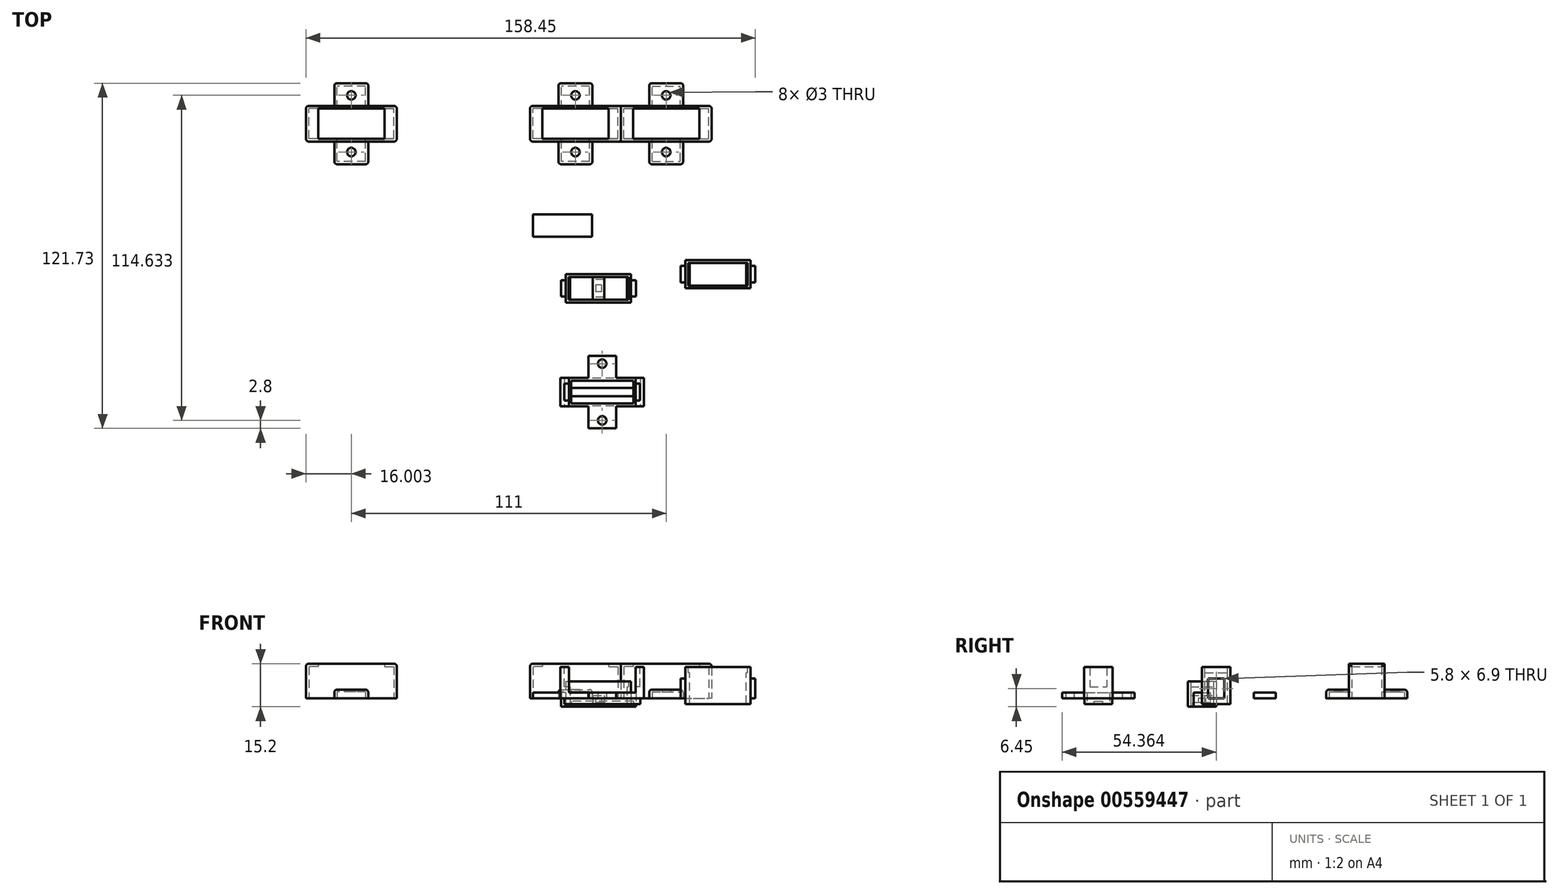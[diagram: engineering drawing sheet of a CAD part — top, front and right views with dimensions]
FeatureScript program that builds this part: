
annotation { "Feature Type Name" : "Feature", "Feature Type Description" : "" }
export const myFeature = defineFeature(function(context is Context, id is Id, definition is map)
    precondition{}
    {
        {
            var Q0;
            Q0=qCreatedBy(makeId("Top.planeOp"),FACE);
            var sketch = newSketch(context, id + "F0", { "sketchPlane" : qUnion([Q0])});
            skLineSegment(sketch, "E0.bottom", {"start": v(-76.87, -5) * mm, "end": v(-104.37, -5) * mm});
            skLineSegment(sketch, "E0.top", {"start": v(-76.87, 5) * mm, "end": v(-104.37, 5) * mm});
            skLineSegment(sketch, "E0.left", {"start": v(-76.87, -5) * mm, "end": v(-76.87, 5) * mm});
            skLineSegment(sketch, "E0.right", {"start": v(-104.37, -5) * mm, "end": v(-104.37, 5) * mm});
            skPoint(sketch, "E0.middle", {"position": v(-90.62, 0) * mm});
            skLineSegment(sketch, "E1.bottom", {"start": v(-87.02, -3.6) * mm, "end": v(-94.22, -3.6) * mm, "construction": true});
            skLineSegment(sketch, "E1.top", {"start": v(-87.02, 3.6) * mm, "end": v(-94.22, 3.6) * mm, "construction": true});
            skLineSegment(sketch, "E1.left", {"start": v(-87.02, -3.6) * mm, "end": v(-87.02, 3.6) * mm, "construction": true});
            skLineSegment(sketch, "E1.right", {"start": v(-94.22, -3.6) * mm, "end": v(-94.22, 3.6) * mm, "construction": true});
            skPoint(sketch, "E2", {"position": v(-90.62, -2.75) * mm});
            skPoint(sketch, "E3", {"position": v(-90.62, 2.75) * mm});
            skLineSegment(sketch, "E4.bottom", {"start": v(-79.62, -4) * mm, "end": v(-101.62, -4) * mm});
            skLineSegment(sketch, "E4.top", {"start": v(-79.62, -1.5) * mm, "end": v(-101.62, -1.5) * mm});
            skLineSegment(sketch, "E4.left", {"start": v(-79.62, -4) * mm, "end": v(-79.62, -1.5) * mm});
            skLineSegment(sketch, "E4.right", {"start": v(-101.62, -4) * mm, "end": v(-101.62, -1.5) * mm});
            skLineSegment(sketch, "E5.bottom", {"start": v(-79.62, 1.5) * mm, "end": v(-101.62, 1.5) * mm});
            skLineSegment(sketch, "E5.top", {"start": v(-79.62, 4) * mm, "end": v(-101.62, 4) * mm});
            skLineSegment(sketch, "E5.left", {"start": v(-79.62, 1.5) * mm, "end": v(-79.62, 4) * mm});
            skLineSegment(sketch, "E5.right", {"start": v(-101.62, 1.5) * mm, "end": v(-101.62, 4) * mm});
            skCircle(sketch, "E6", {"center": v(-90.62, 10) * mm, "radius": 1.5 * mm});
            skCircle(sketch, "E7", {"center": v(-90.62, -10) * mm, "radius": 1.5 * mm});
            skLineSegment(sketch, "E8.bottom", {"start": v(-80.62, -2.5) * mm, "end": v(-85.62, -2.5) * mm, "construction": true});
            skLineSegment(sketch, "E8.top", {"start": v(-80.62, 2.5) * mm, "end": v(-85.62, 2.5) * mm, "construction": true});
            skLineSegment(sketch, "E8.left", {"start": v(-80.62, -2.5) * mm, "end": v(-80.62, 2.5) * mm, "construction": true});
            skLineSegment(sketch, "E8.right", {"start": v(-85.62, -2.5) * mm, "end": v(-85.62, 2.5) * mm, "construction": true});
            skPoint(sketch, "E8.middle", {"position": v(-83.12, 0) * mm});
            skLineSegment(sketch, "E9.bottom", {"start": v(-95.62, -2.5) * mm, "end": v(-100.62, -2.5) * mm, "construction": true});
            skLineSegment(sketch, "E9.top", {"start": v(-95.62, 2.5) * mm, "end": v(-100.62, 2.5) * mm, "construction": true});
            skLineSegment(sketch, "E9.left", {"start": v(-95.62, -2.5) * mm, "end": v(-95.62, 2.5) * mm, "construction": true});
            skLineSegment(sketch, "E9.right", {"start": v(-100.62, -2.5) * mm, "end": v(-100.62, 2.5) * mm, "construction": true});
            skPoint(sketch, "E9.middle", {"position": v(-98.12, 0) * mm});
            skLineSegment(sketch, "E10.bottom", {"start": v(-104.37, 5) * mm, "end": v(-105.37, 5) * mm});
            skLineSegment(sketch, "E10.top", {"start": v(-104.37, -5) * mm, "end": v(-105.37, -5) * mm});
            skLineSegment(sketch, "E10.left", {"start": v(-104.37, 5) * mm, "end": v(-104.37, -5) * mm});
            skLineSegment(sketch, "E10.right", {"start": v(-105.37, 5) * mm, "end": v(-105.37, -5) * mm});
            skLineSegment(sketch, "E11.bottom", {"start": v(-76.87, 5) * mm, "end": v(-75.87, 5) * mm});
            skLineSegment(sketch, "E11.top", {"start": v(-76.87, -5) * mm, "end": v(-75.87, -5) * mm});
            skLineSegment(sketch, "E11.left", {"start": v(-76.87, 5) * mm, "end": v(-76.87, -5) * mm});
            skLineSegment(sketch, "E11.right", {"start": v(-75.87, 5) * mm, "end": v(-75.87, -5) * mm});
            skLineSegment(sketch, "E12.bottom", {"start": v(-95.52, 5) * mm, "end": v(-85.72, 5) * mm});
            skLineSegment(sketch, "E12.top", {"start": v(-95.52, 12.8) * mm, "end": v(-85.72, 12.8) * mm});
            skLineSegment(sketch, "E12.left", {"start": v(-95.52, 5) * mm, "end": v(-95.52, 12.8) * mm});
            skLineSegment(sketch, "E12.right", {"start": v(-85.72, 5) * mm, "end": v(-85.72, 12.8) * mm});
            skLineSegment(sketch, "E13.bottom", {"start": v(-95.52, -5) * mm, "end": v(-85.72, -5) * mm});
            skLineSegment(sketch, "E13.top", {"start": v(-95.52, -12.8) * mm, "end": v(-85.72, -12.8) * mm});
            skLineSegment(sketch, "E13.left", {"start": v(-95.52, -5) * mm, "end": v(-95.52, -12.8) * mm});
            skLineSegment(sketch, "E13.right", {"start": v(-85.72, -5) * mm, "end": v(-85.72, -12.8) * mm});
            skSolve(sketch);
        }
        {
            var Q0;
            Q0=qCreatedBy(makeId("Top.planeOp"),FACE);
            var sketch = newSketch(context, id + "F1", { "sketchPlane" : qUnion([Q0])});
            skLineSegment(sketch, "E14.bottom", {"start": v(-67.93, -50.25) * mm, "end": v(-77.68, -50.25) * mm});
            skLineSegment(sketch, "E14.top", {"start": v(-67.93, -37.75) * mm, "end": v(-77.68, -37.75) * mm});
            skLineSegment(sketch, "E14.left", {"start": v(-67.93, -50.25) * mm, "end": v(-67.93, -37.75) * mm});
            skLineSegment(sketch, "E14.right", {"start": v(-95.43, -50.25) * mm, "end": v(-95.43, -37.75) * mm});
            skPoint(sketch, "E14.middle", {"position": v(-81.68, -44) * mm});
            skCircle(sketch, "E15", {"center": v(-81.68, -34) * mm, "radius": 1.5 * mm});
            skCircle(sketch, "E16", {"center": v(-81.68, -54) * mm, "radius": 1.5 * mm});
            skLineSegment(sketch, "E17.0", {"start": v(-66.93, -51.25) * mm, "end": v(-76.68, -51.25) * mm});
            skLineSegment(sketch, "E17.1", {"start": v(-66.93, -51.25) * mm, "end": v(-66.93, -36.75) * mm});
            skLineSegment(sketch, "E17.2", {"start": v(-66.93, -36.75) * mm, "end": v(-76.68, -36.75) * mm});
            skLineSegment(sketch, "E17.3", {"start": v(-96.43, -51.25) * mm, "end": v(-96.43, -36.75) * mm});
            skLineSegment(sketch, "E18.top", {"start": v(-86.68, -30.75) * mm, "end": v(-76.68, -30.75) * mm});
            skLineSegment(sketch, "E18.left", {"start": v(-86.68, -36.75) * mm, "end": v(-86.68, -30.75) * mm});
            skLineSegment(sketch, "E18.right", {"start": v(-76.68, -36.75) * mm, "end": v(-76.68, -30.75) * mm});
            skLineSegment(sketch, "E19.top", {"start": v(-86.68, -57.25) * mm, "end": v(-76.68, -57.25) * mm});
            skLineSegment(sketch, "E19.left", {"start": v(-86.68, -51.25) * mm, "end": v(-86.68, -57.25) * mm});
            skLineSegment(sketch, "E19.right", {"start": v(-76.68, -51.25) * mm, "end": v(-76.68, -57.25) * mm});
            skPoint(sketch, "E20", {"position": v(-81.68, -30.75) * mm});
            skLineSegment(sketch, "E21.bottom", {"start": v(-86.68, -57.25) * mm, "end": v(-85.68, -57.25) * mm});
            skLineSegment(sketch, "E21.left", {"start": v(-86.68, -57.25) * mm, "end": v(-86.68, -51.25) * mm});
            skLineSegment(sketch, "E21.right", {"start": v(-85.68, -56.25) * mm, "end": v(-85.68, -50.25) * mm});
            skLineSegment(sketch, "E22.bottom", {"start": v(-76.68, -57.25) * mm, "end": v(-77.68, -57.25) * mm});
            skLineSegment(sketch, "E22.left", {"start": v(-76.68, -57.25) * mm, "end": v(-76.68, -51.25) * mm});
            skLineSegment(sketch, "E22.right", {"start": v(-77.68, -56.25) * mm, "end": v(-77.68, -50.25) * mm});
            skLineSegment(sketch, "E23.bottom", {"start": v(-85.68, -57.25) * mm, "end": v(-77.68, -57.25) * mm});
            skLineSegment(sketch, "E23.top", {"start": v(-85.68, -56.25) * mm, "end": v(-77.68, -56.25) * mm});
            skLineSegment(sketch, "E24.trimOffspring", {"start": v(-86.68, -51.25) * mm, "end": v(-96.43, -51.25) * mm});
            skLineSegment(sketch, "E25.trimOffspring", {"start": v(-85.68, -50.25) * mm, "end": v(-95.43, -50.25) * mm});
            skLineSegment(sketch, "E26.left", {"start": v(-86.68, -30.75) * mm, "end": v(-86.68, -36.75) * mm});
            skLineSegment(sketch, "E26.right", {"start": v(-85.68, -31.75) * mm, "end": v(-85.68, -37.75) * mm});
            skLineSegment(sketch, "E27.left", {"start": v(-76.68, -30.75) * mm, "end": v(-76.68, -36.75) * mm});
            skLineSegment(sketch, "E27.right", {"start": v(-77.68, -31.75) * mm, "end": v(-77.68, -37.75) * mm});
            skLineSegment(sketch, "E28.bottom", {"start": v(-85.68, -30.75) * mm, "end": v(-77.68, -30.75) * mm});
            skLineSegment(sketch, "E28.top", {"start": v(-85.68, -31.75) * mm, "end": v(-77.68, -31.75) * mm});
            skLineSegment(sketch, "E29.trimOffspring", {"start": v(-86.68, -36.75) * mm, "end": v(-96.43, -36.75) * mm});
            skLineSegment(sketch, "E30.trimOffspring", {"start": v(-85.68, -37.75) * mm, "end": v(-95.43, -37.75) * mm});
            skLineSegment(sketch, "E31.0", {"start": v(-84.05, 88.33) * mm, "end": v(-84.05, 100.93) * mm});
            skLineSegment(sketch, "E31.1", {"start": v(-106.05, 88.33) * mm, "end": v(-116.05, 88.33) * mm});
            skLineSegment(sketch, "E31.2", {"start": v(-106.05, 80.33) * mm, "end": v(-106.05, 88.33) * mm});
            skLineSegment(sketch, "E31.3", {"start": v(-94.05, 80.33) * mm, "end": v(-106.05, 80.33) * mm});
            skLineSegment(sketch, "E31.4", {"start": v(-94.05, 80.33) * mm, "end": v(-94.05, 88.33) * mm});
            skLineSegment(sketch, "E31.5", {"start": v(-116.05, 88.33) * mm, "end": v(-116.05, 100.93) * mm});
            skLineSegment(sketch, "E31.6", {"start": v(-84.05, 88.33) * mm, "end": v(-94.05, 88.33) * mm});
            skLineSegment(sketch, "E31.7", {"start": v(-106.05, 100.93) * mm, "end": v(-116.05, 100.93) * mm});
            skLineSegment(sketch, "E31.8", {"start": v(-106.05, 100.93) * mm, "end": v(-106.05, 108.93) * mm});
            skLineSegment(sketch, "E31.9", {"start": v(-94.05, 108.93) * mm, "end": v(-106.05, 108.93) * mm});
            skLineSegment(sketch, "E31.10", {"start": v(-94.05, 100.93) * mm, "end": v(-94.05, 108.93) * mm});
            skLineSegment(sketch, "E31.11", {"start": v(-84.05, 100.93) * mm, "end": v(-94.05, 100.93) * mm});
            skPoint(sketch, "E32", {"position": v(-100.05, 94.63) * mm});
            skPoint(sketch, "E32.positionSnap0", {"position": v(-100.05, 108.93) * mm});
            skPoint(sketch, "E32.positionSnap1", {"position": v(-116.05, 94.63) * mm});
            skSolve(sketch);
        }
        {
            var Q0;
            Q0=makeQuery(id+"F0.imprint","IMPRINT",FACE,{"disambiguationData":[TD([[makeQuery(id+"F0.imprint","IMPRINT",EDGE,{"derivedFrom":sQuery(id+"F0.wireOp",EDGE,"E0.bottom")}),-1.0]])]});
            var Q1;
            {var subQ1=sQuery(id+"F0.wireOp",EDGE,"E10.bottom");Q1=makeQuery(id+"F0.imprint","IMPRINT",FACE,{"disambiguationData":[TD([[makeQuery(id+"F0.imprint","IMPRINT",EDGE,{"derivedFrom":subQ1}),1.0]])]});}
            var Q2;
            {var subQ1=sQuery(id+"F0.wireOp",EDGE,"E11.bottom");Q2=makeQuery(id+"F0.imprint","IMPRINT",FACE,{"disambiguationData":[TD([[makeQuery(id+"F0.imprint","IMPRINT",EDGE,{"derivedFrom":subQ1}),-1.0]])]});}
            var Q3;
            Q3=makeQuery(id+"F0.imprint","IMPRINT",FACE,{"disambiguationData":[TD([[makeQuery(id+"F0.imprint","IMPRINT",EDGE,{"derivedFrom":sQuery(id+"F0.wireOp",EDGE,"E6")}),-1.0]])]});
            var Q4;
            Q4=makeQuery(id+"F0.imprint","IMPRINT",FACE,{"disambiguationData":[TD([[makeQuery(id+"F0.imprint","IMPRINT",EDGE,{"derivedFrom":sQuery(id+"F0.wireOp",EDGE,"E7")}),-1.0]])]});
            extrude(context, id + "F2", {"entities" : qUnion([Q0, Q1, Q2, Q3, Q4]), "depth" : 1 * mm});
        }
        {
            var Q0;
            Q0=makeQuery(id+"F2.opExtrude","CAP_FACE",FACE,{"disambiguationData":[OSD([sQuery(id+"F0.wireOp",EDGE,"E0.bottom"),sQuery(id+"F0.wireOp",EDGE,"E0.top"),sQuery(id+"F0.wireOp",EDGE,"E0.left"),sQuery(id+"F0.wireOp",EDGE,"E0.right"),sQuery(id+"F0.wireOp",EDGE,"E4.bottom"),sQuery(id+"F0.wireOp",EDGE,"E4.top"),sQuery(id+"F0.wireOp",EDGE,"E4.left"),sQuery(id+"F0.wireOp",EDGE,"E4.right"),sQuery(id+"F0.wireOp",EDGE,"E5.bottom"),sQuery(id+"F0.wireOp",EDGE,"E5.top"),sQuery(id+"F0.wireOp",EDGE,"E5.left"),sQuery(id+"F0.wireOp",EDGE,"E5.right"),sQuery(id+"F0.wireOp",EDGE,"E6"),sQuery(id+"F0.wireOp",EDGE,"E7")])],"isStart":false});
            var sketch = newSketch(context, id + "F3", { "sketchPlane" : qUnion([Q0])});
            skLineSegment(sketch, "E33.bottom", {"start": v(-105.37, -5) * mm, "end": v(-102.37, -5) * mm});
            skLineSegment(sketch, "E33.top", {"start": v(-105.37, 5) * mm, "end": v(-102.37, 5) * mm});
            skLineSegment(sketch, "E33.left", {"start": v(-105.37, -5) * mm, "end": v(-105.37, 5) * mm});
            skLineSegment(sketch, "E33.right", {"start": v(-102.37, -5) * mm, "end": v(-102.37, 5) * mm});
            skLineSegment(sketch, "E34.bottom", {"start": v(-75.87, 5) * mm, "end": v(-78.87, 5) * mm});
            skLineSegment(sketch, "E34.top", {"start": v(-75.87, -5) * mm, "end": v(-78.87, -5) * mm});
            skLineSegment(sketch, "E34.left", {"start": v(-75.87, 5) * mm, "end": v(-75.87, -5) * mm});
            skLineSegment(sketch, "E34.right", {"start": v(-78.87, 5) * mm, "end": v(-78.87, -5) * mm});
            skSolve(sketch);
        }
        {
            var Q0;
            Q0=makeQuery(id+"F1.imprint","IMPRINT",FACE,{"disambiguationData":[TD([[makeQuery(id+"F1.imprint","IMPRINT",EDGE,{"derivedFrom":sQuery(id+"F1.wireOp",EDGE,"E31.0")}),1.0]])]});
            extrude(context, id + "F4", {"entities" : qUnion([Q0]), "depth" : 12.2 * mm});
        }
        {
            var Q0;
            Q0=makeQuery(id+"F4.opExtrude","CAP_FACE",FACE,{"disambiguationData":[OSD([sQuery(id+"F1.wireOp",EDGE,"E31.0"),sQuery(id+"F1.wireOp",EDGE,"E31.1"),sQuery(id+"F1.wireOp",EDGE,"E31.2"),sQuery(id+"F1.wireOp",EDGE,"E31.3"),sQuery(id+"F1.wireOp",EDGE,"E31.4"),sQuery(id+"F1.wireOp",EDGE,"E31.5"),sQuery(id+"F1.wireOp",EDGE,"E31.6"),sQuery(id+"F1.wireOp",EDGE,"E31.7"),sQuery(id+"F1.wireOp",EDGE,"E31.8"),sQuery(id+"F1.wireOp",EDGE,"E31.9"),sQuery(id+"F1.wireOp",EDGE,"E31.10"),sQuery(id+"F1.wireOp",EDGE,"E31.11")])],"isStart":true});
            shell(context, id + "F5", {"entities" : qUnion([Q0]), "thickness" : 1 * mm});
        }
        {
            var Q0;
            Q0=makeQuery(id+"F4.opExtrude","CAP_FACE",FACE,{"disambiguationData":[OSD([sQuery(id+"F1.wireOp",EDGE,"E31.0"),sQuery(id+"F1.wireOp",EDGE,"E31.1"),sQuery(id+"F1.wireOp",EDGE,"E31.2"),sQuery(id+"F1.wireOp",EDGE,"E31.3"),sQuery(id+"F1.wireOp",EDGE,"E31.4"),sQuery(id+"F1.wireOp",EDGE,"E31.5"),sQuery(id+"F1.wireOp",EDGE,"E31.6"),sQuery(id+"F1.wireOp",EDGE,"E31.7"),sQuery(id+"F1.wireOp",EDGE,"E31.8"),sQuery(id+"F1.wireOp",EDGE,"E31.9"),sQuery(id+"F1.wireOp",EDGE,"E31.10"),sQuery(id+"F1.wireOp",EDGE,"E31.11")])],"isStart":false});
            var sketch = newSketch(context, id + "F6", { "sketchPlane" : qUnion([Q0])});
            skLineSegment(sketch, "E35.bottom", {"start": v(-110.05, 109.64) * mm, "end": v(-85.3, 109.64) * mm});
            skLineSegment(sketch, "E35.top", {"start": v(-110.05, 100.93) * mm, "end": v(-85.3, 100.93) * mm});
            skLineSegment(sketch, "E35.left", {"start": v(-110.05, 109.64) * mm, "end": v(-110.05, 100.93) * mm});
            skLineSegment(sketch, "E35.right", {"start": v(-85.3, 109.64) * mm, "end": v(-85.3, 100.93) * mm});
            skLineSegment(sketch, "E36.bottom", {"start": v(-110.05, 88.33) * mm, "end": v(-90.05, 88.33) * mm});
            skLineSegment(sketch, "E36.top", {"start": v(-110.05, 79.54) * mm, "end": v(-90.05, 79.54) * mm});
            skLineSegment(sketch, "E36.left", {"start": v(-110.05, 88.33) * mm, "end": v(-110.05, 79.54) * mm});
            skLineSegment(sketch, "E36.right", {"start": v(-90.05, 88.33) * mm, "end": v(-90.05, 79.54) * mm});
            skSolve(sketch);
        }
        {
            var Q0;
            Q0=makeQuery(id+"F6.imprint","IMPRINT",FACE,{"disambiguationData":[TD([[makeQuery(id+"F6.imprint","IMPRINT",EDGE,{"derivedFrom":sQuery(id+"F6.wireOp",EDGE,"E36.top")}),1.0]])]});
            var Q1;
            Q1=makeQuery(id+"F6.imprint","IMPRINT",FACE,{"disambiguationData":[TD([[makeQuery(id+"F6.imprint","IMPRINT",EDGE,{"derivedFrom":sQuery(id+"F6.wireOp",EDGE,"E35.bottom")}),-1.0]])]});
            var Q2;
            {var subQ1=makeQuery(id+"F4.opExtrude","CAP_EDGE",EDGE,{"disambiguationData":[OSD([sQuery(id+"F1.wireOp",EDGE,"E31.8")])],"isStart":false});Q2=makeQuery(id+"F6.imprint","IMPRINT",FACE,{"disambiguationData":[TD([[makeQuery(id+"F6.imprint","IMPRINT",EDGE,{"derivedFrom":subQ1}),-1.0]])]});}
            var Q3;
            {var subQ1=makeQuery(id+"F4.opExtrude","CAP_EDGE",EDGE,{"disambiguationData":[OSD([sQuery(id+"F1.wireOp",EDGE,"E31.2")])],"isStart":false});Q3=makeQuery(id+"F6.imprint","IMPRINT",FACE,{"disambiguationData":[TD([[makeQuery(id+"F6.imprint","IMPRINT",EDGE,{"derivedFrom":subQ1}),-1.0]])]});}
            extrude(context, id + "F7", {"entities" : qUnion([Q0, Q1, Q2, Q3]), "operationType" : NewBodyOperationType.REMOVE, "oppositeDirection" : true, "depth" : 11.2 * mm});
        }
        {
            var Q0;
            Q0=makeQuery(id+"F5.opShell","OFFSET_FACE",FACE,{"disambiguationData":[OSD([sQuery(id+"F1.wireOp",EDGE,"E31.4")])]});
            var sketch = newSketch(context, id + "F8", { "sketchPlane" : qUnion([Q0])});
            skLineSegment(sketch, "E37.bottom", {"start": v(-88.33, 11.2) * mm, "end": v(-89.33, 11.2) * mm});
            skLineSegment(sketch, "E37.top", {"start": v(-88.33, 0) * mm, "end": v(-89.33, 0) * mm});
            skLineSegment(sketch, "E37.left", {"start": v(-88.33, 11.2) * mm, "end": v(-88.33, 0) * mm});
            skLineSegment(sketch, "E37.right", {"start": v(-89.33, 11.2) * mm, "end": v(-89.33, 0) * mm});
            skSolve(sketch);
        }
        {
            var Q0;
            Q0=makeQuery(id+"F5.opShell","OFFSET_FACE",FACE,{"disambiguationData":[OSD([sQuery(id+"F1.wireOp",EDGE,"E31.10")])]});
            var sketch = newSketch(context, id + "F9", { "sketchPlane" : qUnion([Q0])});
            skLineSegment(sketch, "E38.bottom", {"start": v(-99.93, 11.2) * mm, "end": v(-100.93, 11.2) * mm});
            skLineSegment(sketch, "E38.top", {"start": v(-99.93, 0) * mm, "end": v(-100.93, 0) * mm});
            skLineSegment(sketch, "E38.left", {"start": v(-99.93, 11.2) * mm, "end": v(-99.93, 0) * mm});
            skLineSegment(sketch, "E38.right", {"start": v(-100.93, 11.2) * mm, "end": v(-100.93, 0) * mm});
            skSolve(sketch);
        }
        {
            var Q0;
            Q0=qSketchRegion(id+"F9",true);
            var Q1;
            {var subQ1=sQuery(id+"F8.wireOp",EDGE,"E37.bottom");Q1=makeQuery(id+"F8.imprint","IMPRINT",FACE,{"disambiguationData":[TD([[makeQuery(id+"F8.imprint","IMPRINT",EDGE,{"derivedFrom":subQ1}),1.0]])]});}
            extrude(context, id + "F10", {"entities" : qUnion([Q0, Q1]), "operationType" : NewBodyOperationType.ADD, "depth" : 16 * mm});
        }
        {
            var Q0;
            Q0=makeQuery(id+"F4.opExtrude","CAP_FACE",FACE,{"disambiguationData":[OSD([sQuery(id+"F1.wireOp",EDGE,"E31.0"),sQuery(id+"F1.wireOp",EDGE,"E31.1"),sQuery(id+"F1.wireOp",EDGE,"E31.2"),sQuery(id+"F1.wireOp",EDGE,"E31.3"),sQuery(id+"F1.wireOp",EDGE,"E31.4"),sQuery(id+"F1.wireOp",EDGE,"E31.5"),sQuery(id+"F1.wireOp",EDGE,"E31.6"),sQuery(id+"F1.wireOp",EDGE,"E31.7"),sQuery(id+"F1.wireOp",EDGE,"E31.8"),sQuery(id+"F1.wireOp",EDGE,"E31.9"),sQuery(id+"F1.wireOp",EDGE,"E31.10"),sQuery(id+"F1.wireOp",EDGE,"E31.11")])],"isStart":false});
            var sketch = newSketch(context, id + "F11", { "sketchPlane" : qUnion([Q0])});
            skLineSegment(sketch, "E39.bottom", {"start": v(-85.05, 89.33) * mm, "end": v(-115.05, 89.33) * mm});
            skLineSegment(sketch, "E39.top", {"start": v(-85.05, 99.93) * mm, "end": v(-115.05, 99.93) * mm});
            skLineSegment(sketch, "E39.left", {"start": v(-85.05, 89.33) * mm, "end": v(-85.05, 99.93) * mm});
            skLineSegment(sketch, "E39.right", {"start": v(-115.05, 89.33) * mm, "end": v(-115.05, 99.93) * mm});
            skPoint(sketch, "E39.middle", {"position": v(-100.05, 94.63) * mm});
            skPoint(sketch, "E40.positionSnap0", {"position": v(-100.05, 101.88) * mm});
            skPoint(sketch, "E40.positionSnap1", {"position": v(-116.05, 94.63) * mm});
            skSolve(sketch);
        }
        {
            var Q0;
            Q0=makeQuery(id+"F11.imprint","IMPRINT",FACE,{"disambiguationData":[TD([[makeQuery(id+"F11.imprint","IMPRINT",EDGE,{"derivedFrom":sQuery(id+"F11.wireOp",EDGE,"E39.bottom")}),-1.0]])]});
            extrude(context, id + "F12", {"entities" : qUnion([Q0]), "operationType" : NewBodyOperationType.REMOVE, "oppositeDirection" : true, "depth" : 25 * mm});
        }
        {
            var Q0;
            Q0=makeQuery(id+"F7.boolean.opBoolean","COPY",FACE,{"derivedFrom":makeQuery(id+"F7.opExtrude","CAP_FACE",FACE,{"disambiguationData":[OSD([sQuery(id+"F6.wireOp",EDGE,"E35.bottom"),sQuery(id+"F6.wireOp",EDGE,"E35.top"),sQuery(id+"F6.wireOp",EDGE,"E35.left"),sQuery(id+"F6.wireOp",EDGE,"E35.right")])],"isStart":false})});
            var sketch = newSketch(context, id + "F13", { "sketchPlane" : qUnion([Q0])});
            skLineSegment(sketch, "E41.bottom", {"start": v(-106.05, 108.93) * mm, "end": v(-94.05, 108.93) * mm});
            skLineSegment(sketch, "E41.top", {"start": v(-106.05, 100.93) * mm, "end": v(-94.05, 100.93) * mm});
            skLineSegment(sketch, "E41.left", {"start": v(-106.05, 108.93) * mm, "end": v(-106.05, 100.93) * mm});
            skLineSegment(sketch, "E41.right", {"start": v(-94.05, 108.93) * mm, "end": v(-94.05, 100.93) * mm});
            skLineSegment(sketch, "E42.bottom", {"start": v(-106.05, 80.33) * mm, "end": v(-94.05, 80.33) * mm});
            skLineSegment(sketch, "E42.top", {"start": v(-106.05, 88.33) * mm, "end": v(-94.05, 88.33) * mm});
            skLineSegment(sketch, "E42.left", {"start": v(-106.05, 80.33) * mm, "end": v(-106.05, 88.33) * mm});
            skLineSegment(sketch, "E42.right", {"start": v(-94.05, 80.33) * mm, "end": v(-94.05, 88.33) * mm});
            skCircle(sketch, "E43", {"center": v(-100.05, 104.63) * mm, "radius": 1.5 * mm});
            skPoint(sketch, "E43.centerSnap0", {"position": v(-100.05, 108.93) * mm});
            skCircle(sketch, "E44", {"center": v(-100.05, 84.63) * mm, "radius": 1.5 * mm});
            skCircle(sketch, "E45", {"center": v(-100.05, 84.63) * mm, "radius": 2.75 * mm, "construction": true});
            skCircle(sketch, "E46", {"center": v(-100.05, 104.63) * mm, "radius": 2.75 * mm, "construction": true});
            skSolve(sketch);
        }
        {
            var Q0;
            Q0=makeQuery(id+"F13.imprint","IMPRINT",FACE,{"disambiguationData":[TD([[makeQuery(id+"F13.imprint","IMPRINT",EDGE,{"derivedFrom":sQuery(id+"F13.wireOp",EDGE,"E43")}),-1.0]])]});
            var Q1;
            Q1=makeQuery(id+"F13.imprint","IMPRINT",FACE,{"disambiguationData":[TD([[makeQuery(id+"F13.imprint","IMPRINT",EDGE,{"derivedFrom":sQuery(id+"F13.wireOp",EDGE,"E41.bottom")}),1.0]])]});
            var Q2;
            Q2=makeQuery(id+"F13.imprint","IMPRINT",FACE,{"disambiguationData":[TD([[makeQuery(id+"F13.imprint","IMPRINT",EDGE,{"derivedFrom":sQuery(id+"F13.wireOp",EDGE,"E42.bottom")}),1.0]])]});
            extrude(context, id + "F14", {"entities" : qUnion([Q0, Q1, Q2]), "operationType" : NewBodyOperationType.ADD, "depth" : 2 * mm});
        }
        {
            var Q0;
            Q0=makeQuery(id+"F1.imprint","IMPRINT",FACE,{"disambiguationData":[TD([[makeQuery(id+"F1.imprint","IMPRINT",EDGE,{"derivedFrom":sQuery(id+"F1.wireOp",EDGE,"E31.0")}),1.0]])]});
            var sketch = newSketch(context, id + "F15", { "sketchPlane" : qUnion([Q0])});
            skLineSegment(sketch, "E47.bottom", {"start": v(-105.05, 81.33) * mm, "end": v(-95.05, 81.33) * mm});
            skLineSegment(sketch, "E47.top", {"start": v(-105.05, 107.93) * mm, "end": v(-95.05, 107.93) * mm});
            skLineSegment(sketch, "E47.left", {"start": v(-105.05, 81.33) * mm, "end": v(-105.05, 107.93) * mm});
            skLineSegment(sketch, "E47.right", {"start": v(-95.05, 81.33) * mm, "end": v(-95.05, 107.93) * mm});
            skPoint(sketch, "E48.0", {"position": v(-105.05, 107.93) * mm});
            skSolve(sketch);
        }
        {
            var Q0;
            Q0=makeQuery(id+"F15.imprint","IMPRINT",FACE,{"disambiguationData":[TD([[makeQuery(id+"F15.imprint","IMPRINT",EDGE,{"derivedFrom":sQuery(id+"F15.wireOp",EDGE,"E47.bottom")}),1.0]])]});
            extrude(context, id + "F16", {"entities" : qUnion([Q0]), "operationType" : NewBodyOperationType.REMOVE, "depth" : 2.2 * mm});
        }
        {
            var Q0;
            Q0=makeQuery(id+"F12.boolean.opBoolean","MERGE",FACE,{"derivedFrom":[makeQuery(id+"F5.opShell","OFFSET_FACE",FACE,{"disambiguationData":[OSD([sQuery(id+"F1.wireOp",EDGE,"E31.5")])]}),makeQuery(id+"F12.opExtrude","SWEPT_FACE",FACE,{"disambiguationData":[OSD([sQuery(id+"F11.wireOp",EDGE,"E39.right")])]})]});
            var sketch = newSketch(context, id + "F17", { "sketchPlane" : qUnion([Q0])});
            skLineSegment(sketch, "E49.bottom", {"start": v(89.33, 11.2) * mm, "end": v(99.93, 11.2) * mm});
            skLineSegment(sketch, "E49.top", {"start": v(89.33, 12.2) * mm, "end": v(99.93, 12.2) * mm});
            skLineSegment(sketch, "E49.left", {"start": v(89.33, 11.2) * mm, "end": v(89.33, 12.2) * mm});
            skLineSegment(sketch, "E49.right", {"start": v(99.93, 11.2) * mm, "end": v(99.93, 12.2) * mm});
            skSolve(sketch);
        }
        {
            var Q0;
            Q0=makeQuery(id+"F12.boolean.opBoolean","MERGE",FACE,{"derivedFrom":[makeQuery(id+"F5.opShell","OFFSET_FACE",FACE,{"disambiguationData":[OSD([sQuery(id+"F1.wireOp",EDGE,"E31.0")])]}),makeQuery(id+"F12.opExtrude","SWEPT_FACE",FACE,{"disambiguationData":[OSD([sQuery(id+"F11.wireOp",EDGE,"E39.left")])]})]});
            var sketch = newSketch(context, id + "F18", { "sketchPlane" : qUnion([Q0])});
            skLineSegment(sketch, "E50.bottom", {"start": v(-99.93, 11.2) * mm, "end": v(-89.33, 11.2) * mm});
            skLineSegment(sketch, "E50.top", {"start": v(-99.93, 12.2) * mm, "end": v(-89.33, 12.2) * mm});
            skLineSegment(sketch, "E50.left", {"start": v(-99.93, 11.2) * mm, "end": v(-99.93, 12.2) * mm});
            skLineSegment(sketch, "E50.right", {"start": v(-89.33, 11.2) * mm, "end": v(-89.33, 12.2) * mm});
            skSolve(sketch);
        }
        {
            var Q0;
            Q0=makeQuery(id+"F17.imprint","IMPRINT",FACE,{"disambiguationData":[TD([[makeQuery(id+"F17.imprint","IMPRINT",EDGE,{"derivedFrom":sQuery(id+"F17.wireOp",EDGE,"E49.bottom")}),1.0]])]});
            extrude(context, id + "F19", {"entities" : qUnion([Q0]), "operationType" : NewBodyOperationType.ADD, "depth" : 3.3 * mm});
        }
        {
            var Q0;
            Q0=makeQuery(id+"F18.imprint","IMPRINT",FACE,{"disambiguationData":[TD([[makeQuery(id+"F18.imprint","IMPRINT",EDGE,{"derivedFrom":sQuery(id+"F18.wireOp",EDGE,"E50.bottom")}),1.0]])]});
            extrude(context, id + "F20", {"entities" : qUnion([Q0]), "operationType" : NewBodyOperationType.ADD, "depth" : 3.3 * mm});
        }
        {
            var Q0;
            Q0=makeQuery(id+"F0.imprint","IMPRINT",FACE,{"disambiguationData":[TD([[makeQuery(id+"F0.imprint","IMPRINT",EDGE,{"derivedFrom":sQuery(id+"F0.wireOp",EDGE,"E4.bottom")}),1.0]])]});
            var sketch = newSketch(context, id + "F21", { "sketchPlane" : qUnion([Q0])});
            skPoint(sketch, "E51.0", {"position": v(-90.62, 0) * mm});
            skLineSegment(sketch, "E52.bottom", {"start": v(-77.22, 4.9) * mm, "end": v(-104.02, 4.9) * mm});
            skLineSegment(sketch, "E52.top", {"start": v(-77.22, -4.9) * mm, "end": v(-104.02, -4.9) * mm});
            skLineSegment(sketch, "E52.left", {"start": v(-77.22, 4.9) * mm, "end": v(-77.22, -4.9) * mm});
            skLineSegment(sketch, "E52.right", {"start": v(-104.02, 4.9) * mm, "end": v(-104.02, -4.9) * mm});
            skPoint(sketch, "E53.0", {"position": v(-101.62, -4) * mm});
            skPoint(sketch, "E53.1", {"position": v(-79.62, -1.5) * mm});
            skPoint(sketch, "E53.2", {"position": v(-101.62, 1.5) * mm});
            skPoint(sketch, "E53.3", {"position": v(-79.62, 4) * mm});
            skLineSegment(sketch, "E54.bottom", {"start": v(-101.62, -4) * mm, "end": v(-79.62, -4) * mm});
            skLineSegment(sketch, "E54.top", {"start": v(-101.62, -1.5) * mm, "end": v(-79.62, -1.5) * mm});
            skLineSegment(sketch, "E54.left", {"start": v(-101.62, -4) * mm, "end": v(-101.62, -1.5) * mm});
            skLineSegment(sketch, "E54.right", {"start": v(-79.62, -4) * mm, "end": v(-79.62, -1.5) * mm});
            skLineSegment(sketch, "E55.bottom", {"start": v(-101.62, 1.5) * mm, "end": v(-79.62, 1.5) * mm});
            skLineSegment(sketch, "E55.top", {"start": v(-101.62, 4) * mm, "end": v(-79.62, 4) * mm});
            skLineSegment(sketch, "E55.left", {"start": v(-101.62, 1.5) * mm, "end": v(-101.62, 4) * mm});
            skLineSegment(sketch, "E55.right", {"start": v(-79.62, 1.5) * mm, "end": v(-79.62, 4) * mm});
            skSolve(sketch);
        }
        {
            var Q0;
            Q0=qSketchRegion(id+"F21",true);
            extrude(context, id + "F22", {"entities" : qUnion([Q0]), "operationType" : NewBodyOperationType.ADD, "oppositeDirection" : true, "depth" : 2 * mm});
        }
        {
            var Q0;
            Q0=makeQuery(id+"F2.opExtrude","CAP_FACE",FACE,{"disambiguationData":[OSD([sQuery(id+"F0.wireOp",EDGE,"E0.bottom"),sQuery(id+"F0.wireOp",EDGE,"E0.top"),sQuery(id+"F0.wireOp",EDGE,"E4.bottom"),sQuery(id+"F0.wireOp",EDGE,"E4.top"),sQuery(id+"F0.wireOp",EDGE,"E4.left"),sQuery(id+"F0.wireOp",EDGE,"E4.right"),sQuery(id+"F0.wireOp",EDGE,"E5.bottom"),sQuery(id+"F0.wireOp",EDGE,"E5.top"),sQuery(id+"F0.wireOp",EDGE,"E5.left"),sQuery(id+"F0.wireOp",EDGE,"E5.right"),sQuery(id+"F0.wireOp",EDGE,"E6"),sQuery(id+"F0.wireOp",EDGE,"E7"),sQuery(id+"F0.wireOp",EDGE,"E10.bottom"),sQuery(id+"F0.wireOp",EDGE,"E10.top"),sQuery(id+"F0.wireOp",EDGE,"E10.right"),sQuery(id+"F0.wireOp",EDGE,"E11.bottom"),sQuery(id+"F0.wireOp",EDGE,"E11.top"),sQuery(id+"F0.wireOp",EDGE,"E11.right"),sQuery(id+"F0.wireOp",EDGE,"E12.top"),sQuery(id+"F0.wireOp",EDGE,"E12.left"),sQuery(id+"F0.wireOp",EDGE,"E12.right"),sQuery(id+"F0.wireOp",EDGE,"E13.top"),sQuery(id+"F0.wireOp",EDGE,"E13.left"),sQuery(id+"F0.wireOp",EDGE,"E13.right")])],"isStart":false});
            var sketch = newSketch(context, id + "F23", { "sketchPlane" : qUnion([Q0])});
            skLineSegment(sketch, "E56.bottom", {"start": v(-101.62, 4) * mm, "end": v(-79.62, 4) * mm});
            skLineSegment(sketch, "E56.top", {"start": v(-101.62, -4) * mm, "end": v(-79.62, -4) * mm});
            skLineSegment(sketch, "E56.left", {"start": v(-101.62, 4) * mm, "end": v(-101.62, -4) * mm});
            skLineSegment(sketch, "E56.right", {"start": v(-79.62, 4) * mm, "end": v(-79.62, -4) * mm});
            skSolve(sketch);
        }
        {
            var Q0;
            Q0=qSketchRegion(id+"F23",true);
            extrude(context, id + "F24", {"entities" : qUnion([Q0]), "operationType" : NewBodyOperationType.REMOVE, "oppositeDirection" : true, "depth" : 2 * mm});
        }
        {
            var Q0;
            Q0=makeQuery(id+"F3.imprint","IMPRINT",FACE,{"disambiguationData":[TD([[makeQuery(id+"F3.imprint","IMPRINT",EDGE,{"derivedFrom":sQuery(id+"F3.wireOp",EDGE,"E33.bottom")}),-1.0]])]});
            var Q1;
            Q1=makeQuery(id+"F3.imprint","IMPRINT",FACE,{"disambiguationData":[TD([[makeQuery(id+"F3.imprint","IMPRINT",EDGE,{"derivedFrom":sQuery(id+"F3.wireOp",EDGE,"E34.bottom")}),1.0]])]});
            extrude(context, id + "F25", {"entities" : qUnion([Q0, Q1]), "operationType" : NewBodyOperationType.ADD, "depth" : 10 * mm});
        }
        {
            var Q0;
            Q0=makeQuery(id+"F25.opExtrude","CAP_FACE",FACE,{"disambiguationData":[OSD([sQuery(id+"F3.wireOp",EDGE,"E33.bottom"),sQuery(id+"F3.wireOp",EDGE,"E33.top"),sQuery(id+"F3.wireOp",EDGE,"E33.left"),sQuery(id+"F3.wireOp",EDGE,"E33.right")])],"isStart":false});
            var sketch = newSketch(context, id + "F26", { "sketchPlane" : qUnion([Q0])});
            skPoint(sketch, "E57.0", {"position": v(-90.62, 0) * mm});
            skLineSegment(sketch, "E58.bottom", {"start": v(-77.27, -3) * mm, "end": v(-103.97, -3) * mm});
            skLineSegment(sketch, "E58.top", {"start": v(-77.27, 3) * mm, "end": v(-103.97, 3) * mm});
            skLineSegment(sketch, "E58.left", {"start": v(-77.27, -3) * mm, "end": v(-77.27, 3) * mm});
            skLineSegment(sketch, "E58.right", {"start": v(-103.97, -3) * mm, "end": v(-103.97, 3) * mm});
            skSolve(sketch);
        }
        {
            var Q0;
            {var subQ0=sQuery(id+"F26.wireOp",EDGE,"E58.left");Q0=makeQuery(id+"F26.imprint","IMPRINT",FACE,{"disambiguationData":[TD([[makeQuery(id+"F26.imprint","IMPRINT",EDGE,{"derivedFrom":subQ0}),1.0]])]});}
            var Q1;
            {var subQ0=sQuery(id+"F26.wireOp",EDGE,"E58.right");Q1=makeQuery(id+"F26.imprint","IMPRINT",FACE,{"disambiguationData":[TD([[makeQuery(id+"F26.imprint","IMPRINT",EDGE,{"derivedFrom":subQ0}),-1.0]])]});}
            extrude(context, id + "F27", {"entities" : qUnion([Q0, Q1]), "operationType" : NewBodyOperationType.REMOVE, "oppositeDirection" : true, "depth" : 7 * mm});
        }
        {
            var Q0;
            Q0=qCreatedBy(makeId("Top.planeOp"),FACE);
            var sketch = newSketch(context, id + "F28", { "sketchPlane" : qUnion([Q0])});
            skLineSegment(sketch, "E59.bottom", {"start": v(-80.42, 30.57) * mm, "end": v(-103.42, 30.57) * mm});
            skLineSegment(sketch, "E59.top", {"start": v(-80.42, 42.57) * mm, "end": v(-103.42, 42.57) * mm});
            skLineSegment(sketch, "E59.left", {"start": v(-80.42, 30.57) * mm, "end": v(-80.42, 42.57) * mm});
            skLineSegment(sketch, "E59.right", {"start": v(-103.42, 30.57) * mm, "end": v(-103.42, 42.57) * mm});
            skPoint(sketch, "E59.middle", {"position": v(-91.92, 36.57) * mm});
            skLineSegment(sketch, "E60.bottom", {"start": v(-103.42, 33.67) * mm, "end": v(-105.12, 33.67) * mm});
            skLineSegment(sketch, "E60.top", {"start": v(-103.42, 39.47) * mm, "end": v(-105.12, 39.47) * mm});
            skLineSegment(sketch, "E60.left", {"start": v(-103.42, 33.67) * mm, "end": v(-103.42, 39.47) * mm});
            skLineSegment(sketch, "E60.right", {"start": v(-105.12, 33.67) * mm, "end": v(-105.12, 39.47) * mm});
            skPoint(sketch, "E60.middle", {"position": v(-104.27, 36.57) * mm});
            skLineSegment(sketch, "E61.bottom", {"start": v(-78.72, 33.67) * mm, "end": v(-80.42, 33.67) * mm});
            skLineSegment(sketch, "E61.top", {"start": v(-78.72, 39.47) * mm, "end": v(-80.42, 39.47) * mm});
            skLineSegment(sketch, "E61.left", {"start": v(-78.72, 33.67) * mm, "end": v(-78.72, 39.47) * mm});
            skLineSegment(sketch, "E61.right", {"start": v(-80.42, 33.67) * mm, "end": v(-80.42, 39.47) * mm});
            skPoint(sketch, "E61.middle", {"position": v(-79.57, 36.57) * mm});
            skLineSegment(sketch, "E62.bottom", {"start": v(-93.92, 32.57) * mm, "end": v(-101.92, 32.57) * mm});
            skLineSegment(sketch, "E62.top", {"start": v(-93.92, 40.57) * mm, "end": v(-101.92, 40.57) * mm});
            skLineSegment(sketch, "E62.left", {"start": v(-93.92, 32.57) * mm, "end": v(-93.92, 40.57) * mm});
            skLineSegment(sketch, "E62.right", {"start": v(-101.92, 32.57) * mm, "end": v(-101.92, 40.57) * mm});
            skLineSegment(sketch, "E63.bottom", {"start": v(-81.92, 32.57) * mm, "end": v(-89.92, 32.57) * mm});
            skLineSegment(sketch, "E63.top", {"start": v(-81.92, 40.57) * mm, "end": v(-89.92, 40.57) * mm});
            skLineSegment(sketch, "E63.left", {"start": v(-81.92, 32.57) * mm, "end": v(-81.92, 40.57) * mm});
            skLineSegment(sketch, "E63.right", {"start": v(-89.92, 32.57) * mm, "end": v(-89.92, 40.57) * mm});
            skSolve(sketch);
        }
        {
            var Q0;
            {var subQ3=sQuery(id+"F28.wireOp",EDGE,"E59.bottom");Q0=makeQuery(id+"F28.imprint","IMPRINT",FACE,{"disambiguationData":[TD([[makeQuery(id+"F28.imprint","IMPRINT",EDGE,{"derivedFrom":subQ3}),-1.0]])]});}
            var Q1;
            Q1=makeQuery(id+"F28.imprint","IMPRINT",FACE,{"disambiguationData":[TD([[makeQuery(id+"F28.imprint","IMPRINT",EDGE,{"derivedFrom":sQuery(id+"F28.wireOp",EDGE,"E60.bottom")}),-1.0]])]});
            var Q2;
            Q2=makeQuery(id+"F28.imprint","IMPRINT",FACE,{"disambiguationData":[TD([[makeQuery(id+"F28.imprint","IMPRINT",EDGE,{"derivedFrom":sQuery(id+"F28.wireOp",EDGE,"E61.bottom")}),-1.0]])]});
            extrude(context, id + "F29", {"entities" : qUnion([Q0, Q1, Q2]), "depth" : 1 * mm});
        }
        {
            var Q0;
            Q0=makeQuery(id+"F29.opExtrude","CAP_FACE",FACE,{"disambiguationData":[OSD([sQuery(id+"F28.wireOp",EDGE,"E59.bottom"),sQuery(id+"F28.wireOp",EDGE,"E59.top"),sQuery(id+"F28.wireOp",EDGE,"E59.left"),sQuery(id+"F28.wireOp",EDGE,"E59.right"),sQuery(id+"F28.wireOp",EDGE,"E60.bottom"),sQuery(id+"F28.wireOp",EDGE,"E60.top"),sQuery(id+"F28.wireOp",EDGE,"E60.right"),sQuery(id+"F28.wireOp",EDGE,"E61.bottom"),sQuery(id+"F28.wireOp",EDGE,"E61.top"),sQuery(id+"F28.wireOp",EDGE,"E61.left"),sQuery(id+"F28.wireOp",EDGE,"E62.bottom"),sQuery(id+"F28.wireOp",EDGE,"E62.top"),sQuery(id+"F28.wireOp",EDGE,"E62.left"),sQuery(id+"F28.wireOp",EDGE,"E62.right"),sQuery(id+"F28.wireOp",EDGE,"E63.bottom"),sQuery(id+"F28.wireOp",EDGE,"E63.top"),sQuery(id+"F28.wireOp",EDGE,"E63.left"),sQuery(id+"F28.wireOp",EDGE,"E63.right")])],"isStart":false});
            var sketch = newSketch(context, id + "F30", { "sketchPlane" : qUnion([Q0])});
            skLineSegment(sketch, "E64.bottom", {"start": v(-103.42, 41.57) * mm, "end": v(-80.42, 41.57) * mm});
            skLineSegment(sketch, "E64.top", {"start": v(-103.42, 31.57) * mm, "end": v(-80.42, 31.57) * mm});
            skLineSegment(sketch, "E64.left", {"start": v(-103.42, 41.57) * mm, "end": v(-103.42, 31.57) * mm});
            skLineSegment(sketch, "E64.right", {"start": v(-80.42, 41.57) * mm, "end": v(-80.42, 31.57) * mm});
            skLineSegment(sketch, "E65.0", {"start": v(-102.42, 40.57) * mm, "end": v(-81.42, 40.57) * mm});
            skLineSegment(sketch, "E66.0", {"start": v(-102.42, 40.57) * mm, "end": v(-102.42, 32.57) * mm});
            skLineSegment(sketch, "E67.0", {"start": v(-81.42, 40.57) * mm, "end": v(-81.42, 32.57) * mm});
            skLineSegment(sketch, "E67.1", {"start": v(-102.42, 32.57) * mm, "end": v(-81.42, 32.57) * mm});
            skSolve(sketch);
        }
        {
            var Q0;
            {var subQ13=sQuery(id+"F30.wireOp",EDGE,"E64.bottom");Q0=makeQuery(id+"F30.imprint","IMPRINT",FACE,{"disambiguationData":[TD([[makeQuery(id+"F30.imprint","IMPRINT",EDGE,{"derivedFrom":subQ13}),-1.0]])]});}
            extrude(context, id + "F31", {"entities" : qUnion([Q0]), "operationType" : NewBodyOperationType.ADD, "depth" : 5 * mm});
        }
        {
            var Q0;
            {var subQ0=sQuery(id+"F28.wireOp",EDGE,"E63.bottom");var subQ1=sQuery(id+"F28.wireOp",EDGE,"E62.top");var subQ2=sQuery(id+"F28.wireOp",EDGE,"E63.top");var subQ3=sQuery(id+"F28.wireOp",EDGE,"E62.bottom");var subQ4=sQuery(id+"F28.wireOp",EDGE,"E63.left");Q0=makeQuery(id+"F31.boolean.opBoolean","SPLIT",FACE,{"disambiguationData":[TD([makeQuery(id+"F29.opExtrude","SWEPT_FACE",FACE,{"disambiguationData":[OSD([subQ4])]})])],"derivedFrom":makeQuery(id+"F29.opExtrude","CAP_FACE",FACE,{"disambiguationData":[OSD([sQuery(id+"F28.wireOp",EDGE,"E59.bottom"),sQuery(id+"F28.wireOp",EDGE,"E59.top"),sQuery(id+"F28.wireOp",EDGE,"E59.left"),sQuery(id+"F28.wireOp",EDGE,"E59.right"),sQuery(id+"F28.wireOp",EDGE,"E60.bottom"),sQuery(id+"F28.wireOp",EDGE,"E60.top"),sQuery(id+"F28.wireOp",EDGE,"E60.right"),sQuery(id+"F28.wireOp",EDGE,"E61.bottom"),sQuery(id+"F28.wireOp",EDGE,"E61.top"),sQuery(id+"F28.wireOp",EDGE,"E61.left"),subQ3,subQ1,sQuery(id+"F28.wireOp",EDGE,"E62.left"),sQuery(id+"F28.wireOp",EDGE,"E62.right"),subQ0,subQ2,subQ4,sQuery(id+"F28.wireOp",EDGE,"E63.right")])],"isStart":false})});}
            var Q1;
            {var subQ0=sQuery(id+"F28.wireOp",EDGE,"E63.bottom");var subQ1=sQuery(id+"F28.wireOp",EDGE,"E62.right");var subQ2=sQuery(id+"F28.wireOp",EDGE,"E62.top");var subQ3=sQuery(id+"F28.wireOp",EDGE,"E62.bottom");var subQ4=sQuery(id+"F28.wireOp",EDGE,"E63.top");Q1=makeQuery(id+"F31.boolean.opBoolean","SPLIT",FACE,{"disambiguationData":[TD([makeQuery(id+"F29.opExtrude","SWEPT_FACE",FACE,{"disambiguationData":[OSD([subQ1])]})])],"derivedFrom":makeQuery(id+"F29.opExtrude","CAP_FACE",FACE,{"disambiguationData":[OSD([sQuery(id+"F28.wireOp",EDGE,"E59.bottom"),sQuery(id+"F28.wireOp",EDGE,"E59.top"),sQuery(id+"F28.wireOp",EDGE,"E59.left"),sQuery(id+"F28.wireOp",EDGE,"E59.right"),sQuery(id+"F28.wireOp",EDGE,"E60.bottom"),sQuery(id+"F28.wireOp",EDGE,"E60.top"),sQuery(id+"F28.wireOp",EDGE,"E60.right"),sQuery(id+"F28.wireOp",EDGE,"E61.bottom"),sQuery(id+"F28.wireOp",EDGE,"E61.top"),sQuery(id+"F28.wireOp",EDGE,"E61.left"),subQ3,subQ2,sQuery(id+"F28.wireOp",EDGE,"E62.left"),subQ1,subQ0,subQ4,sQuery(id+"F28.wireOp",EDGE,"E63.left"),sQuery(id+"F28.wireOp",EDGE,"E63.right")])],"isStart":false})});}
            extrude(context, id + "F32", {"entities" : qUnion([Q0, Q1]), "operationType" : NewBodyOperationType.ADD, "depth" : 3 * mm});
        }
        {
            var Q0;
            Q0=makeQuery(id+"F2.opExtrude","CAP_FACE",FACE,{"disambiguationData":[OSD([sQuery(id+"F0.wireOp",EDGE,"E0.bottom"),sQuery(id+"F0.wireOp",EDGE,"E0.top"),sQuery(id+"F0.wireOp",EDGE,"E4.bottom"),sQuery(id+"F0.wireOp",EDGE,"E4.top"),sQuery(id+"F0.wireOp",EDGE,"E4.left"),sQuery(id+"F0.wireOp",EDGE,"E4.right"),sQuery(id+"F0.wireOp",EDGE,"E5.bottom"),sQuery(id+"F0.wireOp",EDGE,"E5.top"),sQuery(id+"F0.wireOp",EDGE,"E5.left"),sQuery(id+"F0.wireOp",EDGE,"E5.right"),sQuery(id+"F0.wireOp",EDGE,"E6"),sQuery(id+"F0.wireOp",EDGE,"E7"),sQuery(id+"F0.wireOp",EDGE,"E10.bottom"),sQuery(id+"F0.wireOp",EDGE,"E10.top"),sQuery(id+"F0.wireOp",EDGE,"E10.right"),sQuery(id+"F0.wireOp",EDGE,"E11.bottom"),sQuery(id+"F0.wireOp",EDGE,"E11.top"),sQuery(id+"F0.wireOp",EDGE,"E11.right"),sQuery(id+"F0.wireOp",EDGE,"E12.top"),sQuery(id+"F0.wireOp",EDGE,"E12.left"),sQuery(id+"F0.wireOp",EDGE,"E12.right"),sQuery(id+"F0.wireOp",EDGE,"E13.top"),sQuery(id+"F0.wireOp",EDGE,"E13.left"),sQuery(id+"F0.wireOp",EDGE,"E13.right")])],"isStart":false});
            extrude(context, id + "F33", {"entities" : qUnion([Q0]), "operationType" : NewBodyOperationType.ADD, "depth" : 1 * mm});
        }
        {
            var Q0;
            Q0=makeQuery(id+"F31.opExtrude","CAP_FACE",FACE,{"disambiguationData":[OSD([sQuery(id+"F30.wireOp",EDGE,"E64.bottom"),sQuery(id+"F30.wireOp",EDGE,"E64.top"),sQuery(id+"F30.wireOp",EDGE,"E64.left"),sQuery(id+"F30.wireOp",EDGE,"E64.right"),sQuery(id+"F30.wireOp",EDGE,"E65.0"),sQuery(id+"F30.wireOp",EDGE,"E66.0"),sQuery(id+"F30.wireOp",EDGE,"E67.0"),sQuery(id+"F30.wireOp",EDGE,"E67.1")])],"isStart":false});
            var sketch = newSketch(context, id + "F34", { "sketchPlane" : qUnion([Q0])});
            skLineSegment(sketch, "E68.bottom", {"start": v(-103.42, 41.57) * mm, "end": v(-80.42, 41.57) * mm});
            skLineSegment(sketch, "E68.top", {"start": v(-103.42, 42.57) * mm, "end": v(-80.42, 42.57) * mm});
            skLineSegment(sketch, "E68.left", {"start": v(-103.42, 41.57) * mm, "end": v(-103.42, 42.57) * mm});
            skLineSegment(sketch, "E68.right", {"start": v(-80.42, 41.57) * mm, "end": v(-80.42, 42.57) * mm});
            skLineSegment(sketch, "E69.bottom", {"start": v(-103.42, 31.57) * mm, "end": v(-80.42, 31.57) * mm});
            skLineSegment(sketch, "E69.top", {"start": v(-103.42, 30.57) * mm, "end": v(-80.42, 30.57) * mm});
            skLineSegment(sketch, "E69.left", {"start": v(-103.42, 31.57) * mm, "end": v(-103.42, 30.57) * mm});
            skLineSegment(sketch, "E69.right", {"start": v(-80.42, 31.57) * mm, "end": v(-80.42, 30.57) * mm});
            skSolve(sketch);
        }
        {
            var Q0;
            Q0=qSketchRegion(id+"F34",true);
            extrude(context, id + "F35", {"entities" : qUnion([Q0]), "operationType" : NewBodyOperationType.REMOVE, "oppositeDirection" : true, "depth" : 10 * mm});
        }
        {
            var Q0;
            Q0=makeQuery(id+"F14.opExtrude","CAP_EDGE",EDGE,{"disambiguationData":[OSD([sQuery(id+"F13.wireOp",EDGE,"E42.left")])],"isStart":false});
            var Q1;
            Q1=makeQuery(id+"F14.opExtrude","CAP_EDGE",EDGE,{"disambiguationData":[OSD([sQuery(id+"F13.wireOp",EDGE,"E42.right")])],"isStart":false});
            var Q2;
            Q2=makeQuery(id+"F14.opExtrude","CAP_EDGE",EDGE,{"disambiguationData":[OSD([sQuery(id+"F13.wireOp",EDGE,"E42.bottom")])],"isStart":false});
            var Q3;
            Q3=makeQuery(id+"F14.boolean.opBoolean","MERGE",EDGE,{"derivedFrom":[makeQuery(id+"F4.opExtrude","SWEPT_EDGE",EDGE,{"disambiguationData":[OSD([sQuery(id+"F1.wireOp",EDGE,"E31.2"),sQuery(id+"F1.wireOp",EDGE,"E31.3")])]}),makeQuery(id+"F14.opExtrude","SWEPT_EDGE",EDGE,{"disambiguationData":[OSD([sQuery(id+"F13.wireOp",EDGE,"E42.bottom"),sQuery(id+"F13.wireOp",EDGE,"E42.left")])]})]});
            var Q4;
            Q4=makeQuery(id+"F14.boolean.opBoolean","MERGE",EDGE,{"derivedFrom":[makeQuery(id+"F4.opExtrude","SWEPT_EDGE",EDGE,{"disambiguationData":[OSD([sQuery(id+"F1.wireOp",EDGE,"E31.3"),sQuery(id+"F1.wireOp",EDGE,"E31.4")])]}),makeQuery(id+"F14.opExtrude","SWEPT_EDGE",EDGE,{"disambiguationData":[OSD([sQuery(id+"F13.wireOp",EDGE,"E42.bottom"),sQuery(id+"F13.wireOp",EDGE,"E42.right")])]})]});
            var Q5;
            Q5=makeQuery(id+"F14.opExtrude","CAP_EDGE",EDGE,{"disambiguationData":[OSD([sQuery(id+"F13.wireOp",EDGE,"E41.right")])],"isStart":false});
            var Q6;
            Q6=makeQuery(id+"F14.boolean.opBoolean","MERGE",EDGE,{"derivedFrom":[makeQuery(id+"F4.opExtrude","SWEPT_EDGE",EDGE,{"disambiguationData":[OSD([sQuery(id+"F1.wireOp",EDGE,"E31.9"),sQuery(id+"F1.wireOp",EDGE,"E31.10")])]}),makeQuery(id+"F14.opExtrude","SWEPT_EDGE",EDGE,{"disambiguationData":[OSD([sQuery(id+"F13.wireOp",EDGE,"E41.bottom"),sQuery(id+"F13.wireOp",EDGE,"E41.right")])]})]});
            var Q7;
            Q7=makeQuery(id+"F14.opExtrude","CAP_EDGE",EDGE,{"disambiguationData":[OSD([sQuery(id+"F13.wireOp",EDGE,"E41.bottom")])],"isStart":false});
            var Q8;
            Q8=makeQuery(id+"F14.opExtrude","CAP_EDGE",EDGE,{"disambiguationData":[OSD([sQuery(id+"F13.wireOp",EDGE,"E41.left")])],"isStart":false});
            var Q9;
            Q9=makeQuery(id+"F14.boolean.opBoolean","MERGE",EDGE,{"derivedFrom":[makeQuery(id+"F4.opExtrude","SWEPT_EDGE",EDGE,{"disambiguationData":[OSD([sQuery(id+"F1.wireOp",EDGE,"E31.8"),sQuery(id+"F1.wireOp",EDGE,"E31.9")])]}),makeQuery(id+"F14.opExtrude","SWEPT_EDGE",EDGE,{"disambiguationData":[OSD([sQuery(id+"F13.wireOp",EDGE,"E41.bottom"),sQuery(id+"F13.wireOp",EDGE,"E41.left")])]})]});
            fillet(context, id + "F36", {"entities" : qUnion([Q0, Q1, Q2, Q3, Q4, Q5, Q6, Q7, Q8, Q9]), "radius" : 1 * mm, "tangentPropagation" : true, "allowEdgeOverflow" : false});
        }
        {
            var Q0;
            Q0=makeQuery(id+"F4.opExtrude","SWEPT_BODY",BODY,{"disambiguationData":[OSD([sQuery(id+"F1.wireOp",EDGE,"E31.0"),sQuery(id+"F1.wireOp",EDGE,"E31.1"),sQuery(id+"F1.wireOp",EDGE,"E31.2"),sQuery(id+"F1.wireOp",EDGE,"E31.3"),sQuery(id+"F1.wireOp",EDGE,"E31.4"),sQuery(id+"F1.wireOp",EDGE,"E31.5"),sQuery(id+"F1.wireOp",EDGE,"E31.6"),sQuery(id+"F1.wireOp",EDGE,"E31.7"),sQuery(id+"F1.wireOp",EDGE,"E31.8"),sQuery(id+"F1.wireOp",EDGE,"E31.9"),sQuery(id+"F1.wireOp",EDGE,"E31.10"),sQuery(id+"F1.wireOp",EDGE,"E31.11")])]});
            var Q1;
            Q1=makeQuery(id+"F7.boolean.opBoolean","MERGE",EDGE,{"derivedFrom":[makeQuery(id+"F4.opExtrude","CAP_EDGE",EDGE,{"disambiguationData":[OSD([sQuery(id+"F1.wireOp",EDGE,"E31.1")])],"isStart":false}),makeQuery(id+"F4.opExtrude","CAP_EDGE",EDGE,{"disambiguationData":[OSD([sQuery(id+"F1.wireOp",EDGE,"E31.6")])],"isStart":false}),makeQuery(id+"F7.opExtrude","CAP_EDGE",EDGE,{"disambiguationData":[OSD([sQuery(id+"F6.wireOp",EDGE,"E36.bottom")])],"isStart":true})]});
            transform(context, id + "F37", {"entities" : qUnion([Q0]), "transformType" : TransformType.TRANSLATION_3D, "dx" : -79 * mm, "dy" : 0 * mm, "dz" : 0 * mm, "makeCopy" : true});
        }
        {
            var Q0;
            Q0=makeQuery(id+"F37.opPattern","COPY",EDGE,{"derivedFrom":makeQuery(id+"F4.opExtrude","SWEPT_EDGE",EDGE,{"disambiguationData":[OSD([sQuery(id+"F1.wireOp",EDGE,"E31.1"),sQuery(id+"F1.wireOp",EDGE,"E31.5")])]}),"instanceName":"1"});
            var Q1;
            Q1=makeQuery(id+"F37.opPattern","COPY",EDGE,{"derivedFrom":makeQuery(id+"F4.opExtrude","SWEPT_EDGE",EDGE,{"disambiguationData":[OSD([sQuery(id+"F1.wireOp",EDGE,"E31.5"),sQuery(id+"F1.wireOp",EDGE,"E31.7")])]}),"instanceName":"1"});
            var Q2;
            Q2=makeQuery(id+"F37.opPattern","COPY",EDGE,{"derivedFrom":makeQuery(id+"F4.opExtrude","SWEPT_EDGE",EDGE,{"disambiguationData":[OSD([sQuery(id+"F1.wireOp",EDGE,"E31.0"),sQuery(id+"F1.wireOp",EDGE,"E31.6")])]}),"instanceName":"1"});
            var Q3;
            Q3=makeQuery(id+"F37.opPattern","COPY",EDGE,{"derivedFrom":makeQuery(id+"F4.opExtrude","SWEPT_EDGE",EDGE,{"disambiguationData":[OSD([sQuery(id+"F1.wireOp",EDGE,"E31.0"),sQuery(id+"F1.wireOp",EDGE,"E31.11")])]}),"instanceName":"1"});
            var Q4;
            Q4=makeQuery(id+"F37.opPattern","COPY",EDGE,{"derivedFrom":makeQuery(id+"F4.opExtrude","CAP_EDGE",EDGE,{"disambiguationData":[OSD([sQuery(id+"F1.wireOp",EDGE,"E31.5")])],"isStart":false}),"instanceName":"1"});
            var Q5;
            Q5=makeQuery(id+"F37.opPattern","COPY",EDGE,{"derivedFrom":makeQuery(id+"F7.boolean.opBoolean","MERGE",EDGE,{"derivedFrom":[makeQuery(id+"F4.opExtrude","CAP_EDGE",EDGE,{"disambiguationData":[OSD([sQuery(id+"F1.wireOp",EDGE,"E31.1")])],"isStart":false}),makeQuery(id+"F4.opExtrude","CAP_EDGE",EDGE,{"disambiguationData":[OSD([sQuery(id+"F1.wireOp",EDGE,"E31.6")])],"isStart":false}),makeQuery(id+"F7.opExtrude","CAP_EDGE",EDGE,{"disambiguationData":[OSD([sQuery(id+"F6.wireOp",EDGE,"E36.bottom")])],"isStart":true})]}),"instanceName":"1"});
            var Q6;
            Q6=makeQuery(id+"F37.opPattern","COPY",EDGE,{"derivedFrom":makeQuery(id+"F7.boolean.opBoolean","MERGE",EDGE,{"derivedFrom":[makeQuery(id+"F4.opExtrude","CAP_EDGE",EDGE,{"disambiguationData":[OSD([sQuery(id+"F1.wireOp",EDGE,"E31.7")])],"isStart":false}),makeQuery(id+"F4.opExtrude","CAP_EDGE",EDGE,{"disambiguationData":[OSD([sQuery(id+"F1.wireOp",EDGE,"E31.11")])],"isStart":false}),makeQuery(id+"F7.opExtrude","CAP_EDGE",EDGE,{"disambiguationData":[OSD([sQuery(id+"F6.wireOp",EDGE,"E35.top")])],"isStart":true})]}),"instanceName":"1"});
            var Q7;
            Q7=makeQuery(id+"F37.opPattern","COPY",EDGE,{"derivedFrom":makeQuery(id+"F4.opExtrude","CAP_EDGE",EDGE,{"disambiguationData":[OSD([sQuery(id+"F1.wireOp",EDGE,"E31.0")])],"isStart":false}),"instanceName":"1"});
            fillet(context, id + "F38", {"entities" : qUnion([Q0, Q1, Q2, Q3, Q4, Q5, Q6, Q7]), "radius" : 1 * mm, "tangentPropagation" : true, "allowEdgeOverflow" : false});
        }
        {
            var Q0;
            Q0=makeQuery(id+"F4.opExtrude","SWEPT_BODY",BODY,{"disambiguationData":[OSD([sQuery(id+"F1.wireOp",EDGE,"E31.0"),sQuery(id+"F1.wireOp",EDGE,"E31.1"),sQuery(id+"F1.wireOp",EDGE,"E31.2"),sQuery(id+"F1.wireOp",EDGE,"E31.3"),sQuery(id+"F1.wireOp",EDGE,"E31.4"),sQuery(id+"F1.wireOp",EDGE,"E31.5"),sQuery(id+"F1.wireOp",EDGE,"E31.6"),sQuery(id+"F1.wireOp",EDGE,"E31.7"),sQuery(id+"F1.wireOp",EDGE,"E31.8"),sQuery(id+"F1.wireOp",EDGE,"E31.9"),sQuery(id+"F1.wireOp",EDGE,"E31.10"),sQuery(id+"F1.wireOp",EDGE,"E31.11")])]});
            var Q1;
            Q1=makeQuery(id+"F4.opExtrude","SWEPT_FACE",FACE,{"disambiguationData":[OSD([sQuery(id+"F1.wireOp",EDGE,"E31.0")])]});
            mirror(context, id + "F39", {"operationType" : NewBodyOperationType.ADD, "entities" : qUnion([Q0]), "mirrorPlane" : qUnion([Q1])});
        }
        {
            var Q0;
            Q0=makeQuery(id+"F4.opExtrude","SWEPT_EDGE",EDGE,{"disambiguationData":[OSD([sQuery(id+"F1.wireOp",EDGE,"E31.1"),sQuery(id+"F1.wireOp",EDGE,"E31.5")])]});
            var Q1;
            Q1=makeQuery(id+"F4.opExtrude","SWEPT_EDGE",EDGE,{"disambiguationData":[OSD([sQuery(id+"F1.wireOp",EDGE,"E31.5"),sQuery(id+"F1.wireOp",EDGE,"E31.7")])]});
            var Q2;
            Q2=makeQuery(id+"F39.opPattern","COPY",EDGE,{"derivedFrom":makeQuery(id+"F4.opExtrude","SWEPT_EDGE",EDGE,{"disambiguationData":[OSD([sQuery(id+"F1.wireOp",EDGE,"E31.1"),sQuery(id+"F1.wireOp",EDGE,"E31.5")])]}),"instanceName":"1"});
            var Q3;
            Q3=makeQuery(id+"F39.opPattern","COPY",EDGE,{"derivedFrom":makeQuery(id+"F4.opExtrude","SWEPT_EDGE",EDGE,{"disambiguationData":[OSD([sQuery(id+"F1.wireOp",EDGE,"E31.5"),sQuery(id+"F1.wireOp",EDGE,"E31.7")])]}),"instanceName":"1"});
            var Q4;
            Q4=makeQuery(id+"F39.opPattern","COPY",EDGE,{"derivedFrom":makeQuery(id+"F4.opExtrude","CAP_EDGE",EDGE,{"disambiguationData":[OSD([sQuery(id+"F1.wireOp",EDGE,"E31.5")])],"isStart":false}),"instanceName":"1"});
            var Q5;
            {var subQ0=makeQuery(id+"F7.boolean.opBoolean","MERGE",EDGE,{"derivedFrom":[makeQuery(id+"F4.opExtrude","CAP_EDGE",EDGE,{"disambiguationData":[OSD([sQuery(id+"F1.wireOp",EDGE,"E31.1")])],"isStart":false}),makeQuery(id+"F4.opExtrude","CAP_EDGE",EDGE,{"disambiguationData":[OSD([sQuery(id+"F1.wireOp",EDGE,"E31.6")])],"isStart":false}),makeQuery(id+"F7.opExtrude","CAP_EDGE",EDGE,{"disambiguationData":[OSD([sQuery(id+"F6.wireOp",EDGE,"E36.bottom")])],"isStart":true})]});Q5=makeQuery(id+"F39.boolean.opBoolean","MERGE",EDGE,{"derivedFrom":[subQ0,makeQuery(id+"F39.opPattern","COPY",EDGE,{"derivedFrom":subQ0,"instanceName":"1"})]});}
            var Q6;
            {var subQ0=makeQuery(id+"F7.boolean.opBoolean","MERGE",EDGE,{"derivedFrom":[makeQuery(id+"F4.opExtrude","CAP_EDGE",EDGE,{"disambiguationData":[OSD([sQuery(id+"F1.wireOp",EDGE,"E31.7")])],"isStart":false}),makeQuery(id+"F4.opExtrude","CAP_EDGE",EDGE,{"disambiguationData":[OSD([sQuery(id+"F1.wireOp",EDGE,"E31.11")])],"isStart":false}),makeQuery(id+"F7.opExtrude","CAP_EDGE",EDGE,{"disambiguationData":[OSD([sQuery(id+"F6.wireOp",EDGE,"E35.top")])],"isStart":true})]});Q6=makeQuery(id+"F39.boolean.opBoolean","MERGE",EDGE,{"derivedFrom":[subQ0,makeQuery(id+"F39.opPattern","COPY",EDGE,{"derivedFrom":subQ0,"instanceName":"1"})]});}
            var Q7;
            Q7=makeQuery(id+"F4.opExtrude","CAP_EDGE",EDGE,{"disambiguationData":[OSD([sQuery(id+"F1.wireOp",EDGE,"E31.5")])],"isStart":false});
            fillet(context, id + "F40", {"entities" : qUnion([Q0, Q1, Q2, Q3, Q4, Q5, Q6, Q7]), "radius" : 1 * mm, "tangentPropagation" : true, "allowEdgeOverflow" : false});
        }
        {
            var Q0;
            Q0=qCreatedBy(makeId("Top.planeOp"),FACE);
            var sketch = newSketch(context, id + "F41", { "sketchPlane" : qUnion([Q0])});
            skLineSegment(sketch, "E70.bottom", {"start": v(-94.2, 54.83) * mm, "end": v(-115, 54.83) * mm});
            skLineSegment(sketch, "E70.top", {"start": v(-94.2, 62.63) * mm, "end": v(-115, 62.63) * mm});
            skLineSegment(sketch, "E70.left", {"start": v(-94.2, 54.83) * mm, "end": v(-94.2, 62.63) * mm});
            skLineSegment(sketch, "E70.right", {"start": v(-115, 54.83) * mm, "end": v(-115, 62.63) * mm});
            skPoint(sketch, "E70.middle", {"position": v(-104.6, 58.73) * mm});
            skSolve(sketch);
        }
        {
            var Q0;
            Q0=makeQuery(id+"F41.imprint","IMPRINT",FACE,{"disambiguationData":[TD([[makeQuery(id+"F41.imprint","IMPRINT",EDGE,{"derivedFrom":sQuery(id+"F41.wireOp",EDGE,"E70.bottom")}),-1.0]])]});
            extrude(context, id + "F42", {"entities" : qUnion([Q0]), "depth" : 2 * mm});
        }
        {
            var Q0;
            Q0=makeQuery(id+"F29.opExtrude","CAP_FACE",FACE,{"disambiguationData":[OSD([sQuery(id+"F28.wireOp",EDGE,"E59.bottom"),sQuery(id+"F28.wireOp",EDGE,"E59.top"),sQuery(id+"F28.wireOp",EDGE,"E59.left"),sQuery(id+"F28.wireOp",EDGE,"E59.right"),sQuery(id+"F28.wireOp",EDGE,"E60.bottom"),sQuery(id+"F28.wireOp",EDGE,"E60.top"),sQuery(id+"F28.wireOp",EDGE,"E60.right"),sQuery(id+"F28.wireOp",EDGE,"E61.bottom"),sQuery(id+"F28.wireOp",EDGE,"E61.top"),sQuery(id+"F28.wireOp",EDGE,"E61.left"),sQuery(id+"F28.wireOp",EDGE,"E62.bottom"),sQuery(id+"F28.wireOp",EDGE,"E62.top"),sQuery(id+"F28.wireOp",EDGE,"E62.left"),sQuery(id+"F28.wireOp",EDGE,"E62.right"),sQuery(id+"F28.wireOp",EDGE,"E63.bottom"),sQuery(id+"F28.wireOp",EDGE,"E63.top"),sQuery(id+"F28.wireOp",EDGE,"E63.left"),sQuery(id+"F28.wireOp",EDGE,"E63.right")])],"isStart":true});
            extrude(context, id + "F43", {"entities" : qUnion([Q0]), "operationType" : NewBodyOperationType.ADD, "depth" : 3 * mm});
        }
        {
            var Q0;
            Q0=makeQuery(id+"F43.opExtrude","CAP_FACE",FACE,{"disambiguationData":[OSD([sQuery(id+"F28.wireOp",EDGE,"E59.bottom"),sQuery(id+"F28.wireOp",EDGE,"E59.top"),sQuery(id+"F28.wireOp",EDGE,"E59.left"),sQuery(id+"F28.wireOp",EDGE,"E59.right"),sQuery(id+"F28.wireOp",EDGE,"E60.bottom"),sQuery(id+"F28.wireOp",EDGE,"E60.top"),sQuery(id+"F28.wireOp",EDGE,"E60.right"),sQuery(id+"F28.wireOp",EDGE,"E61.bottom"),sQuery(id+"F28.wireOp",EDGE,"E61.top"),sQuery(id+"F28.wireOp",EDGE,"E61.left"),sQuery(id+"F28.wireOp",EDGE,"E62.bottom"),sQuery(id+"F28.wireOp",EDGE,"E62.top"),sQuery(id+"F28.wireOp",EDGE,"E62.left"),sQuery(id+"F28.wireOp",EDGE,"E62.right"),sQuery(id+"F28.wireOp",EDGE,"E63.bottom"),sQuery(id+"F28.wireOp",EDGE,"E63.top"),sQuery(id+"F28.wireOp",EDGE,"E63.left"),sQuery(id+"F28.wireOp",EDGE,"E63.right")])],"isStart":false});
            var sketch = newSketch(context, id + "F44", { "sketchPlane" : qUnion([Q0])});
            skLineSegment(sketch, "E71.bottom", {"start": v(-90.92, -37.82) * mm, "end": v(-92.92, -37.82) * mm, "construction": true});
            skLineSegment(sketch, "E71.top", {"start": v(-90.92, -35.32) * mm, "end": v(-92.92, -35.32) * mm, "construction": true});
            skLineSegment(sketch, "E71.left", {"start": v(-90.92, -37.82) * mm, "end": v(-90.92, -35.32) * mm, "construction": true});
            skLineSegment(sketch, "E71.right", {"start": v(-92.92, -37.82) * mm, "end": v(-92.92, -35.32) * mm, "construction": true});
            skPoint(sketch, "E71.middle", {"position": v(-91.92, -36.57) * mm});
            skPoint(sketch, "E71.middle.positionSnap0", {"position": v(-93.92, -36.57) * mm});
            skPoint(sketch, "E71.middle.positionSnap1", {"position": v(-91.92, -41.57) * mm});
            skPoint(sketch, "E71.centerSnap0", {"position": v(-93.92, -36.57) * mm});
            skPoint(sketch, "E71.centerSnap1", {"position": v(-91.92, -41.57) * mm});
            skLineSegment(sketch, "E72.bottom", {"start": v(-88.77, -39.72) * mm, "end": v(-95.07, -39.72) * mm});
            skLineSegment(sketch, "E72.top", {"start": v(-88.77, -33.42) * mm, "end": v(-95.07, -33.42) * mm});
            skLineSegment(sketch, "E72.left", {"start": v(-88.77, -39.72) * mm, "end": v(-88.77, -33.42) * mm});
            skLineSegment(sketch, "E72.right", {"start": v(-95.07, -39.72) * mm, "end": v(-95.07, -33.42) * mm});
            skSolve(sketch);
        }
        {
            var Q0;
            Q0=qSketchRegion(id+"F44",true);
            extrude(context, id + "F45", {"entities" : qUnion([Q0]), "operationType" : NewBodyOperationType.REMOVE, "oppositeDirection" : true, "depth" : 1.5 * mm});
        }
        {
            var Q0;
            {var subQ17=sQuery(id+"F28.wireOp",EDGE,"E60.bottom");Q0=makeQuery(id+"F44.imprint","IMPRINT",FACE,{"disambiguationData":[TD([[makeQuery(id+"F44.imprint","IMPRINT",EDGE,{"derivedFrom":makeQuery(id+"F43.opExtrude","CAP_EDGE",EDGE,{"disambiguationData":[OSD([subQ17])],"isStart":false})}),1.0]])]});}
            var sketch = newSketch(context, id + "F46", { "sketchPlane" : qUnion([Q0])});
            skPoint(sketch, "E73.0", {"position": v(-91.92, -36.57) * mm});
            skLineSegment(sketch, "E74.bottom", {"start": v(-90.92, -37.82) * mm, "end": v(-92.92, -37.82) * mm});
            skLineSegment(sketch, "E74.top", {"start": v(-90.92, -35.32) * mm, "end": v(-92.92, -35.32) * mm});
            skLineSegment(sketch, "E74.left", {"start": v(-90.92, -37.82) * mm, "end": v(-90.92, -35.32) * mm});
            skLineSegment(sketch, "E74.right", {"start": v(-92.92, -37.82) * mm, "end": v(-92.92, -35.32) * mm});
            skSolve(sketch);
        }
        {
            var Q0;
            Q0=qSketchRegion(id+"F46",true);
            extrude(context, id + "F47", {"entities" : qUnion([Q0]), "operationType" : NewBodyOperationType.REMOVE, "oppositeDirection" : true, "depth" : 3 * mm});
        }
        {
            var Q0;
            {var subQ0=sQuery(id+"F28.wireOp",EDGE,"E60.top");var subQ1=sQuery(id+"F28.wireOp",EDGE,"E60.bottom");var subQ2=sQuery(id+"F28.wireOp",EDGE,"E59.right");var subQ3=sQuery(id+"F28.wireOp",EDGE,"E59.top");var subQ5=sQuery(id+"F28.wireOp",EDGE,"E59.bottom");var subQ6=sQuery(id+"F28.wireOp",EDGE,"E60.right");Q0=makeQuery(id+"F31.boolean.opBoolean","SPLIT",FACE,{"disambiguationData":[TD([makeQuery(id+"F29.opExtrude","SWEPT_FACE",FACE,{"disambiguationData":[OSD([subQ1])]})])],"derivedFrom":makeQuery(id+"F29.opExtrude","CAP_FACE",FACE,{"disambiguationData":[OSD([subQ5,subQ3,sQuery(id+"F28.wireOp",EDGE,"E59.left"),subQ2,subQ1,subQ0,subQ6,sQuery(id+"F28.wireOp",EDGE,"E61.bottom"),sQuery(id+"F28.wireOp",EDGE,"E61.top"),sQuery(id+"F28.wireOp",EDGE,"E61.left"),sQuery(id+"F28.wireOp",EDGE,"E62.bottom"),sQuery(id+"F28.wireOp",EDGE,"E62.top"),sQuery(id+"F28.wireOp",EDGE,"E62.left"),sQuery(id+"F28.wireOp",EDGE,"E62.right"),sQuery(id+"F28.wireOp",EDGE,"E63.bottom"),sQuery(id+"F28.wireOp",EDGE,"E63.top"),sQuery(id+"F28.wireOp",EDGE,"E63.left"),sQuery(id+"F28.wireOp",EDGE,"E63.right")])],"isStart":false})});}
            var Q1;
            {var subQ0=sQuery(id+"F28.wireOp",EDGE,"E61.top");var subQ1=sQuery(id+"F28.wireOp",EDGE,"E61.bottom");var subQ2=sQuery(id+"F28.wireOp",EDGE,"E59.left");var subQ3=sQuery(id+"F28.wireOp",EDGE,"E59.top");var subQ5=sQuery(id+"F28.wireOp",EDGE,"E59.bottom");var subQ6=sQuery(id+"F28.wireOp",EDGE,"E61.left");Q1=makeQuery(id+"F31.boolean.opBoolean","SPLIT",FACE,{"disambiguationData":[TD([makeQuery(id+"F29.opExtrude","SWEPT_FACE",FACE,{"disambiguationData":[OSD([subQ1])]})])],"derivedFrom":makeQuery(id+"F29.opExtrude","CAP_FACE",FACE,{"disambiguationData":[OSD([subQ5,subQ3,subQ2,sQuery(id+"F28.wireOp",EDGE,"E59.right"),sQuery(id+"F28.wireOp",EDGE,"E60.bottom"),sQuery(id+"F28.wireOp",EDGE,"E60.top"),sQuery(id+"F28.wireOp",EDGE,"E60.right"),subQ1,subQ0,subQ6,sQuery(id+"F28.wireOp",EDGE,"E62.bottom"),sQuery(id+"F28.wireOp",EDGE,"E62.top"),sQuery(id+"F28.wireOp",EDGE,"E62.left"),sQuery(id+"F28.wireOp",EDGE,"E62.right"),sQuery(id+"F28.wireOp",EDGE,"E63.bottom"),sQuery(id+"F28.wireOp",EDGE,"E63.top"),sQuery(id+"F28.wireOp",EDGE,"E63.left"),sQuery(id+"F28.wireOp",EDGE,"E63.right")])],"isStart":false})});}
            extrude(context, id + "F48", {"entities" : qUnion([Q0, Q1]), "operationType" : NewBodyOperationType.ADD, "depth" : 1 * mm});
        }
        {
            var Q0;
            Q0=qCreatedBy(makeId("Top.planeOp"),FACE);
            var sketch = newSketch(context, id + "F49", { "sketchPlane" : qUnion([Q0])});
            skLineSegment(sketch, "E75.bottom", {"start": v(-38.3, 36.56) * mm, "end": v(-61.3, 36.56) * mm});
            skLineSegment(sketch, "E75.top", {"start": v(-38.3, 46.56) * mm, "end": v(-61.3, 46.56) * mm});
            skLineSegment(sketch, "E75.left", {"start": v(-38.3, 36.56) * mm, "end": v(-38.3, 46.56) * mm});
            skLineSegment(sketch, "E75.right", {"start": v(-61.3, 36.56) * mm, "end": v(-61.3, 46.56) * mm});
            skPoint(sketch, "E75.middle", {"position": v(-49.8, 41.56) * mm});
            skLineSegment(sketch, "E76.bottom", {"start": v(-61.3, 38.66) * mm, "end": v(-63, 38.66) * mm});
            skLineSegment(sketch, "E76.top", {"start": v(-61.3, 44.46) * mm, "end": v(-63, 44.46) * mm});
            skLineSegment(sketch, "E76.left", {"start": v(-61.3, 38.66) * mm, "end": v(-61.3, 44.46) * mm});
            skLineSegment(sketch, "E76.right", {"start": v(-63, 38.66) * mm, "end": v(-63, 44.46) * mm});
            skLineSegment(sketch, "E77.bottom", {"start": v(-38.3, 44.46) * mm, "end": v(-36.6, 44.46) * mm});
            skLineSegment(sketch, "E77.top", {"start": v(-38.3, 38.66) * mm, "end": v(-36.6, 38.66) * mm});
            skLineSegment(sketch, "E77.left", {"start": v(-38.3, 44.46) * mm, "end": v(-38.3, 38.66) * mm});
            skLineSegment(sketch, "E77.right", {"start": v(-36.6, 44.46) * mm, "end": v(-36.6, 38.66) * mm});
            skLineSegment(sketch, "E78.bottom", {"start": v(-39.3, 37.56) * mm, "end": v(-60.3, 37.56) * mm});
            skLineSegment(sketch, "E78.top", {"start": v(-39.3, 45.56) * mm, "end": v(-60.3, 45.56) * mm});
            skLineSegment(sketch, "E78.left", {"start": v(-39.3, 37.56) * mm, "end": v(-39.3, 45.56) * mm});
            skLineSegment(sketch, "E78.right", {"start": v(-60.3, 37.56) * mm, "end": v(-60.3, 45.56) * mm});
            skSolve(sketch);
        }
        {
            var Q0;
            Q0=makeQuery(id+"F49.imprint","IMPRINT",FACE,{"disambiguationData":[TD([[makeQuery(id+"F49.imprint","IMPRINT",EDGE,{"derivedFrom":sQuery(id+"F49.wireOp",EDGE,"E76.bottom")}),-1.0]])]});
            var Q1;
            {var subQ3=sQuery(id+"F49.wireOp",EDGE,"E75.bottom");Q1=makeQuery(id+"F49.imprint","IMPRINT",FACE,{"disambiguationData":[TD([[makeQuery(id+"F49.imprint","IMPRINT",EDGE,{"derivedFrom":subQ3}),-1.0]])]});}
            var Q2;
            Q2=makeQuery(id+"F49.imprint","IMPRINT",FACE,{"disambiguationData":[TD([[makeQuery(id+"F49.imprint","IMPRINT",EDGE,{"derivedFrom":sQuery(id+"F49.wireOp",EDGE,"E77.bottom")}),-1.0]])]});
            extrude(context, id + "F50", {"entities" : qUnion([Q0, Q1, Q2]), "depth" : 9 * mm});
        }
        {
            var Q0;
            Q0=makeQuery(id+"F50.opExtrude","CAP_FACE",FACE,{"disambiguationData":[OSD([sQuery(id+"F49.wireOp",EDGE,"E75.bottom"),sQuery(id+"F49.wireOp",EDGE,"E75.top"),sQuery(id+"F49.wireOp",EDGE,"E75.left"),sQuery(id+"F49.wireOp",EDGE,"E75.right"),sQuery(id+"F49.wireOp",EDGE,"E76.bottom"),sQuery(id+"F49.wireOp",EDGE,"E76.top"),sQuery(id+"F49.wireOp",EDGE,"E76.right"),sQuery(id+"F49.wireOp",EDGE,"E77.bottom"),sQuery(id+"F49.wireOp",EDGE,"E77.top"),sQuery(id+"F49.wireOp",EDGE,"E77.right"),sQuery(id+"F49.wireOp",EDGE,"E78.bottom"),sQuery(id+"F49.wireOp",EDGE,"E78.top"),sQuery(id+"F49.wireOp",EDGE,"E78.left"),sQuery(id+"F49.wireOp",EDGE,"E78.right")])],"isStart":false});
            var sketch = newSketch(context, id + "F51", { "sketchPlane" : qUnion([Q0])});
            skLineSegment(sketch, "E79.bottom", {"start": v(-61.3, 38.66) * mm, "end": v(-63, 38.66) * mm});
            skLineSegment(sketch, "E79.top", {"start": v(-61.3, 44.46) * mm, "end": v(-63, 44.46) * mm});
            skLineSegment(sketch, "E79.left", {"start": v(-61.3, 38.66) * mm, "end": v(-61.3, 44.46) * mm});
            skLineSegment(sketch, "E79.right", {"start": v(-63, 38.66) * mm, "end": v(-63, 44.46) * mm});
            skLineSegment(sketch, "E80.bottom", {"start": v(-36.6, 38.66) * mm, "end": v(-38.3, 38.66) * mm});
            skLineSegment(sketch, "E80.top", {"start": v(-36.6, 44.46) * mm, "end": v(-38.3, 44.46) * mm});
            skLineSegment(sketch, "E80.left", {"start": v(-36.6, 38.66) * mm, "end": v(-36.6, 44.46) * mm});
            skLineSegment(sketch, "E80.right", {"start": v(-38.3, 38.66) * mm, "end": v(-38.3, 44.46) * mm});
            skSolve(sketch);
        }
        {
            var Q0;
            Q0=qSketchRegion(id+"F51",true);
            extrude(context, id + "F52", {"entities" : qUnion([Q0]), "operationType" : NewBodyOperationType.REMOVE, "oppositeDirection" : true, "depth" : 2.1 * mm});
        }
        {
            var Q0;
            Q0=makeQuery(id+"F50.opExtrude","CAP_FACE",FACE,{"disambiguationData":[OSD([sQuery(id+"F49.wireOp",EDGE,"E75.bottom"),sQuery(id+"F49.wireOp",EDGE,"E75.top"),sQuery(id+"F49.wireOp",EDGE,"E75.left"),sQuery(id+"F49.wireOp",EDGE,"E75.right"),sQuery(id+"F49.wireOp",EDGE,"E76.bottom"),sQuery(id+"F49.wireOp",EDGE,"E76.top"),sQuery(id+"F49.wireOp",EDGE,"E76.right"),sQuery(id+"F49.wireOp",EDGE,"E77.bottom"),sQuery(id+"F49.wireOp",EDGE,"E77.top"),sQuery(id+"F49.wireOp",EDGE,"E77.right"),sQuery(id+"F49.wireOp",EDGE,"E78.bottom"),sQuery(id+"F49.wireOp",EDGE,"E78.top"),sQuery(id+"F49.wireOp",EDGE,"E78.left"),sQuery(id+"F49.wireOp",EDGE,"E78.right")])],"isStart":false});
            extrude(context, id + "F53", {"entities" : qUnion([Q0]), "operationType" : NewBodyOperationType.ADD, "depth" : 2 * mm});
        }
        {
            var Q0;
            Q0=makeQuery(id+"F50.opExtrude","CAP_FACE",FACE,{"disambiguationData":[OSD([sQuery(id+"F49.wireOp",EDGE,"E75.bottom"),sQuery(id+"F49.wireOp",EDGE,"E75.top"),sQuery(id+"F49.wireOp",EDGE,"E75.left"),sQuery(id+"F49.wireOp",EDGE,"E75.right"),sQuery(id+"F49.wireOp",EDGE,"E76.bottom"),sQuery(id+"F49.wireOp",EDGE,"E76.top"),sQuery(id+"F49.wireOp",EDGE,"E76.right"),sQuery(id+"F49.wireOp",EDGE,"E77.bottom"),sQuery(id+"F49.wireOp",EDGE,"E77.top"),sQuery(id+"F49.wireOp",EDGE,"E77.right"),sQuery(id+"F49.wireOp",EDGE,"E78.bottom"),sQuery(id+"F49.wireOp",EDGE,"E78.top"),sQuery(id+"F49.wireOp",EDGE,"E78.left"),sQuery(id+"F49.wireOp",EDGE,"E78.right")])],"isStart":true});
            var sketch = newSketch(context, id + "F54", { "sketchPlane" : qUnion([Q0])});
            skLineSegment(sketch, "E81.bottom", {"start": v(-61.3, -36.56) * mm, "end": v(-38.3, -36.56) * mm});
            skLineSegment(sketch, "E81.top", {"start": v(-61.3, -46.56) * mm, "end": v(-38.3, -46.56) * mm});
            skLineSegment(sketch, "E81.left", {"start": v(-61.3, -36.56) * mm, "end": v(-61.3, -46.56) * mm});
            skLineSegment(sketch, "E81.right", {"start": v(-38.3, -36.56) * mm, "end": v(-38.3, -46.56) * mm});
            skLineSegment(sketch, "E82.bottom", {"start": v(-60.3, -37.56) * mm, "end": v(-39.3, -37.56) * mm});
            skLineSegment(sketch, "E82.top", {"start": v(-60.3, -45.56) * mm, "end": v(-39.3, -45.56) * mm});
            skLineSegment(sketch, "E82.left", {"start": v(-60.3, -37.56) * mm, "end": v(-60.3, -45.56) * mm});
            skLineSegment(sketch, "E82.right", {"start": v(-39.3, -37.56) * mm, "end": v(-39.3, -45.56) * mm});
            skSolve(sketch);
        }
        {
            var Q0;
            {var subQ4=sQuery(id+"F54.wireOp",EDGE,"E81.bottom");Q0=makeQuery(id+"F54.imprint","IMPRINT",FACE,{"disambiguationData":[TD([[makeQuery(id+"F54.imprint","IMPRINT",EDGE,{"derivedFrom":subQ4}),1.0]])]});}
            extrude(context, id + "F55", {"entities" : qUnion([Q0]), "operationType" : NewBodyOperationType.ADD, "depth" : 2 * mm});
        }
        {
            var Q0;
            Q0=makeQuery(id+"F53.opExtrude","CAP_FACE",FACE,{"disambiguationData":[OSD([sQuery(id+"F49.wireOp",EDGE,"E75.bottom"),sQuery(id+"F49.wireOp",EDGE,"E75.top"),sQuery(id+"F49.wireOp",EDGE,"E75.left"),sQuery(id+"F49.wireOp",EDGE,"E75.right"),sQuery(id+"F49.wireOp",EDGE,"E76.bottom"),sQuery(id+"F49.wireOp",EDGE,"E76.top"),sQuery(id+"F49.wireOp",EDGE,"E76.right"),sQuery(id+"F49.wireOp",EDGE,"E77.bottom"),sQuery(id+"F49.wireOp",EDGE,"E77.top"),sQuery(id+"F49.wireOp",EDGE,"E77.right"),sQuery(id+"F49.wireOp",EDGE,"E78.bottom"),sQuery(id+"F49.wireOp",EDGE,"E78.top"),sQuery(id+"F49.wireOp",EDGE,"E78.left"),sQuery(id+"F49.wireOp",EDGE,"E78.right")])],"isStart":false});
            var sketch = newSketch(context, id + "F56", { "sketchPlane" : qUnion([Q0])});
            skLineSegment(sketch, "E83.bottom", {"start": v(-60.3, 45.56) * mm, "end": v(-59.8, 45.56) * mm});
            skLineSegment(sketch, "E83.top", {"start": v(-60.3, 37.56) * mm, "end": v(-59.8, 37.56) * mm});
            skLineSegment(sketch, "E83.left", {"start": v(-60.3, 45.56) * mm, "end": v(-60.3, 37.56) * mm});
            skLineSegment(sketch, "E83.right", {"start": v(-59.8, 45.56) * mm, "end": v(-59.8, 37.56) * mm});
            skLineSegment(sketch, "E84.bottom", {"start": v(-39.3, 37.56) * mm, "end": v(-39.8, 37.56) * mm});
            skLineSegment(sketch, "E84.top", {"start": v(-39.3, 45.56) * mm, "end": v(-39.8, 45.56) * mm});
            skLineSegment(sketch, "E84.left", {"start": v(-39.3, 37.56) * mm, "end": v(-39.3, 45.56) * mm});
            skLineSegment(sketch, "E84.right", {"start": v(-39.8, 37.56) * mm, "end": v(-39.8, 45.56) * mm});
            skSolve(sketch);
        }
        {
            var Q0;
            Q0=qSketchRegion(id+"F56",true);
            extrude(context, id + "F57", {"entities" : qUnion([Q0]), "operationType" : NewBodyOperationType.ADD, "oppositeDirection" : true, "depth" : 13 * mm});
        }
        {
            var Q0;
            Q0=makeQuery(id+"F57.boolean.opBoolean","MERGE",FACE,{"derivedFrom":[makeQuery(id+"F53.opExtrude","CAP_FACE",FACE,{"disambiguationData":[OSD([sQuery(id+"F49.wireOp",EDGE,"E75.bottom"),sQuery(id+"F49.wireOp",EDGE,"E75.top"),sQuery(id+"F49.wireOp",EDGE,"E75.left"),sQuery(id+"F49.wireOp",EDGE,"E75.right"),sQuery(id+"F49.wireOp",EDGE,"E76.bottom"),sQuery(id+"F49.wireOp",EDGE,"E76.top"),sQuery(id+"F49.wireOp",EDGE,"E76.right"),sQuery(id+"F49.wireOp",EDGE,"E77.bottom"),sQuery(id+"F49.wireOp",EDGE,"E77.top"),sQuery(id+"F49.wireOp",EDGE,"E77.right"),sQuery(id+"F49.wireOp",EDGE,"E78.bottom"),sQuery(id+"F49.wireOp",EDGE,"E78.top"),sQuery(id+"F49.wireOp",EDGE,"E78.left"),sQuery(id+"F49.wireOp",EDGE,"E78.right")])],"isStart":false}),makeQuery(id+"F57.opExtrude","CAP_FACE",FACE,{"disambiguationData":[OSD([sQuery(id+"F56.wireOp",EDGE,"E83.bottom"),sQuery(id+"F56.wireOp",EDGE,"E83.top"),sQuery(id+"F56.wireOp",EDGE,"E83.left"),sQuery(id+"F56.wireOp",EDGE,"E83.right")])],"isStart":true}),makeQuery(id+"F57.opExtrude","CAP_FACE",FACE,{"disambiguationData":[OSD([sQuery(id+"F56.wireOp",EDGE,"E84.bottom"),sQuery(id+"F56.wireOp",EDGE,"E84.top"),sQuery(id+"F56.wireOp",EDGE,"E84.left"),sQuery(id+"F56.wireOp",EDGE,"E84.right")])],"isStart":true})]});
            var sketch = newSketch(context, id + "F58", { "sketchPlane" : qUnion([Q0])});
            skLineSegment(sketch, "E85.bottom", {"start": v(-39.3, 37.56) * mm, "end": v(-60.3, 37.56) * mm});
            skLineSegment(sketch, "E85.top", {"start": v(-39.3, 45.56) * mm, "end": v(-60.3, 45.56) * mm});
            skLineSegment(sketch, "E85.left", {"start": v(-39.3, 37.56) * mm, "end": v(-39.3, 45.56) * mm});
            skLineSegment(sketch, "E85.right", {"start": v(-60.3, 37.56) * mm, "end": v(-60.3, 45.56) * mm});
            skPoint(sketch, "E85.middle", {"position": v(-49.8, 41.56) * mm});
            skPoint(sketch, "E85.middle.positionSnap0", {"position": v(-61.3, 41.56) * mm});
            skPoint(sketch, "E85.middle.positionSnap1", {"position": v(-49.8, 46.56) * mm});
            skPoint(sketch, "E85.centerSnap0", {"position": v(-61.3, 41.56) * mm});
            skPoint(sketch, "E85.centerSnap1", {"position": v(-49.8, 46.56) * mm});
            skSolve(sketch);
        }
        {
            var Q0;
            {var subQ2=sQuery(id+"F58.wireOp",EDGE,"E85.right");Q0=makeQuery(id+"F58.imprint","IMPRINT",FACE,{"disambiguationData":[TD([[makeQuery(id+"F58.imprint","IMPRINT",EDGE,{"derivedFrom":subQ2}),-1.0]])]});}
            var Q1;
            {var subQ1=makeQuery(id+"F57.opExtrude","CAP_EDGE",EDGE,{"disambiguationData":[OSD([sQuery(id+"F56.wireOp",EDGE,"E83.right")])],"isStart":true});Q1=makeQuery(id+"F58.imprint","IMPRINT",FACE,{"disambiguationData":[TD([[makeQuery(id+"F58.imprint","IMPRINT",EDGE,{"derivedFrom":subQ1}),1.0]])]});}
            var Q2;
            {var subQ2=sQuery(id+"F58.wireOp",EDGE,"E85.left");Q2=makeQuery(id+"F58.imprint","IMPRINT",FACE,{"disambiguationData":[TD([[makeQuery(id+"F58.imprint","IMPRINT",EDGE,{"derivedFrom":subQ2}),1.0]])]});}
            extrude(context, id + "F59", {"entities" : qUnion([Q0, Q1, Q2]), "operationType" : NewBodyOperationType.REMOVE, "oppositeDirection" : true, "depth" : 2 * mm});
        }
    });
